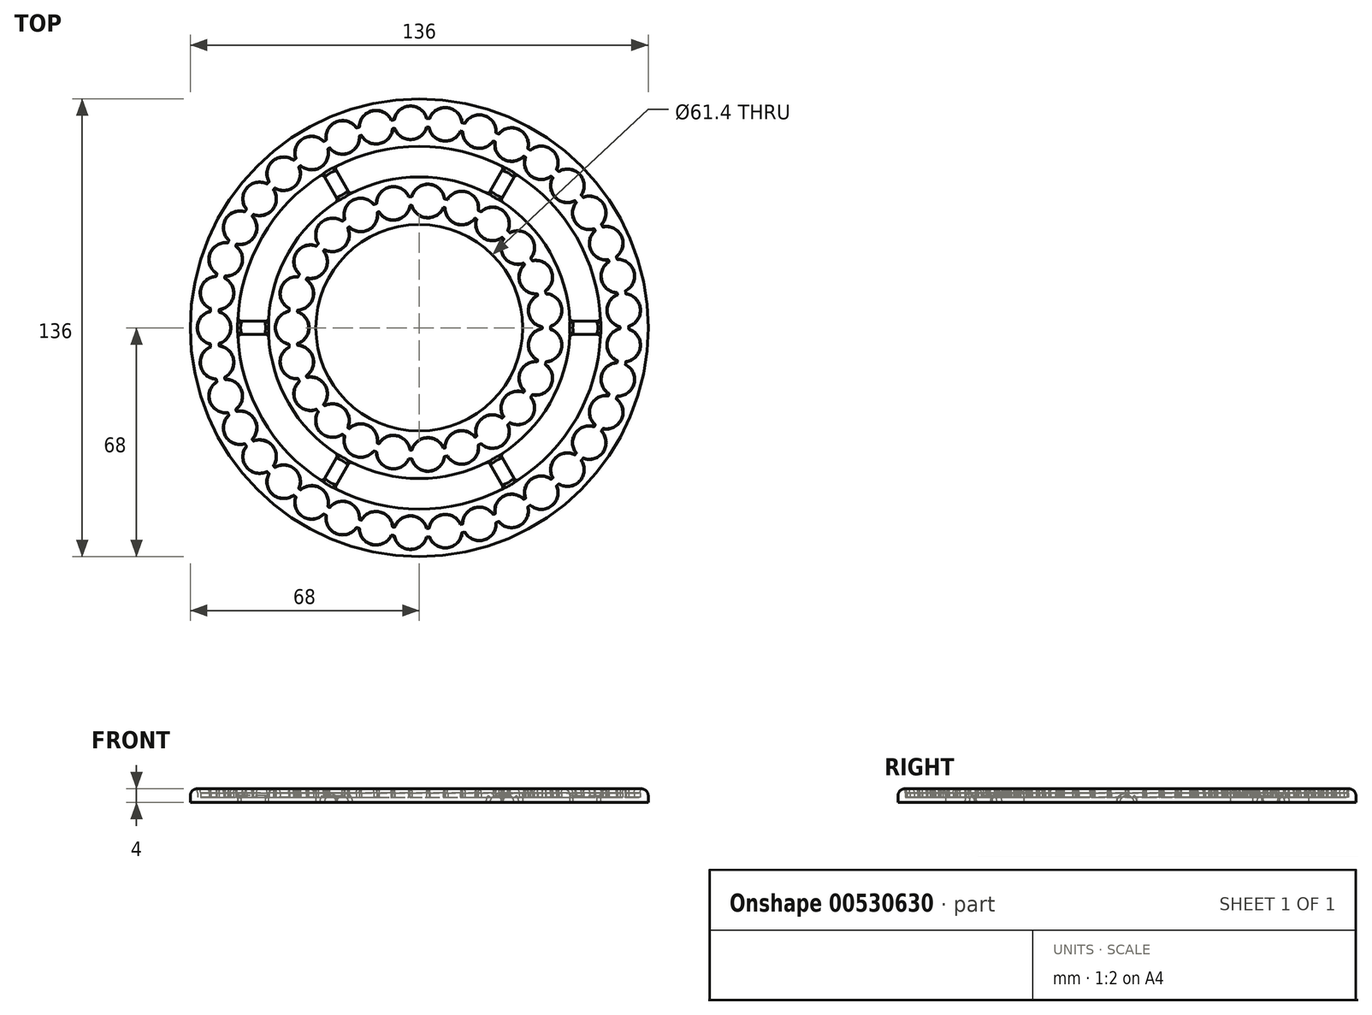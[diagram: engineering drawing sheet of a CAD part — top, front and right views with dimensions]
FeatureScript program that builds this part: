
annotation { "Feature Type Name" : "Feature", "Feature Type Description" : "" }
export const myFeature = defineFeature(function(context is Context, id is Id, definition is map)
    precondition{}
    {
        {
            var Q0;
            Q0=qCreatedBy(makeId("Front.planeOp"),FACE);
            var sketch = newSketch(context, id + "F0", { "sketchPlane" : qUnion([Q0])});
            skPoint(sketch, "E0", {"position": v(-70, 0) * mm});
            skLineSegment(sketch, "E1", {"start": v(-70, 0) * mm, "end": v(-70, 4) * mm});
            skLineSegment(sketch, "E2", {"start": v(-70, 4) * mm, "end": v(-66, 4) * mm});
            skLineSegment(sketch, "E3", {"start": v(-66, 4) * mm, "end": v(-65.85, 2.75) * mm});
            skLineSegment(sketch, "E4", {"start": v(-65.7, 1.5) * mm, "end": v(-56.2, 1.5) * mm});
            skLineSegment(sketch, "E5", {"start": v(-56.05, 2.75) * mm, "end": v(-55.9, 4) * mm});
            skLineSegment(sketch, "E6", {"start": v(-55.9, 4) * mm, "end": v(-42.8, 4) * mm});
            skLineSegment(sketch, "E7", {"start": v(-42.8, 4) * mm, "end": v(-42.65, 2.75) * mm});
            skLineSegment(sketch, "E8", {"start": v(-42.5, 1.5) * mm, "end": v(-33, 1.5) * mm});
            skLineSegment(sketch, "E9", {"start": v(-32.85, 2.75) * mm, "end": v(-32.7, 4) * mm});
            skLineSegment(sketch, "E10", {"start": v(-32.7, 4) * mm, "end": v(-28.7, 4) * mm});
            skLineSegment(sketch, "E11", {"start": v(-28.7, 4) * mm, "end": v(-28.7, 0) * mm});
            skLineSegment(sketch, "E12", {"start": v(-28.7, 0) * mm, "end": v(-70, 0) * mm});
            skPoint(sketch, "E13", {"position": v(-65.85, 2.75) * mm});
            skPoint(sketch, "E14", {"position": v(-32.85, 2.75) * mm});
            skLineSegment(sketch, "E15", {"start": v(-32.85, 2.75) * mm, "end": v(-32.85, 1.5) * mm});
            skLineSegment(sketch, "E16", {"start": v(-32.85, 1.5) * mm, "end": v(-33, 1.5) * mm});
            skLineSegment(sketch, "E17", {"start": v(-42.65, 2.75) * mm, "end": v(-42.65, 1.5) * mm});
            skLineSegment(sketch, "E18", {"start": v(-42.65, 1.5) * mm, "end": v(-42.5, 1.5) * mm});
            skLineSegment(sketch, "E19", {"start": v(-65.85, 2.75) * mm, "end": v(-65.85, 1.5) * mm});
            skLineSegment(sketch, "E20", {"start": v(-65.85, 1.5) * mm, "end": v(-65.7, 1.5) * mm});
            skLineSegment(sketch, "E21", {"start": v(-56.05, 2.75) * mm, "end": v(-56.05, 1.5) * mm});
            skLineSegment(sketch, "E22", {"start": v(-56.05, 1.5) * mm, "end": v(-56.2, 1.5) * mm});
            skLineSegment(sketch, "E23", {"start": v(0, 0) * mm, "end": v(0, 13.47) * mm});
            skLineSegment(sketch, "E24", {"start": v(-66, 4) * mm, "end": v(-32.7, 4) * mm});
            skLineSegment(sketch, "E25", {"start": v(-60.95, 1.5) * mm, "end": v(-60.95, 4) * mm});
            skLineSegment(sketch, "E26", {"start": v(-37.75, 1.5) * mm, "end": v(-37.75, 4) * mm});
            skLineSegment(sketch, "E27", {"start": v(-62.2, 1.5) * mm, "end": v(-62.2, 4) * mm});
            skLineSegment(sketch, "E28", {"start": v(-59.7, 4) * mm, "end": v(-59.7, 1.5) * mm});
            skLineSegment(sketch, "E29", {"start": v(-39, 4) * mm, "end": v(-39, 1.5) * mm});
            skLineSegment(sketch, "E30", {"start": v(-36.5, 4) * mm, "end": v(-36.5, 1.5) * mm});
            skPoint(sketch, "E31", {"position": v(-49.35, 4) * mm});
            skLineSegment(sketch, "E32", {"start": v(-68, 4) * mm, "end": v(-68, 0) * mm});
            skLineSegment(sketch, "E33", {"start": v(-30.7, 4) * mm, "end": v(-30.7, 0) * mm});
            skLineSegment(sketch, "E34", {"start": v(-53.9, 4) * mm, "end": v(-53.9, 2) * mm});
            skLineSegment(sketch, "E35", {"start": v(-53.9, 2) * mm, "end": v(-44.8, 2) * mm});
            skLineSegment(sketch, "E36", {"start": v(-44.8, 2) * mm, "end": v(-44.8, 4) * mm});
            skSolve(sketch);
        }
        {
            var Q0;
            {var subQ2=sQuery(id+"F0.wireOp",EDGE,"E9");Q0=makeQuery(id+"F0.imprint","IMPRINT",FACE,{"disambiguationData":[TD([[makeQuery(id+"F0.imprint","IMPRINT",EDGE,{"derivedFrom":subQ2}),1.0]])]});}
            var Q1;
            {var subQ1=sQuery(id+"F0.wireOp",EDGE,"E5");Q1=makeQuery(id+"F0.imprint","IMPRINT",FACE,{"disambiguationData":[TD([[makeQuery(id+"F0.imprint","IMPRINT",EDGE,{"derivedFrom":subQ1}),1.0]])]});}
            var Q2;
            {var subQ4=sQuery(id+"F0.wireOp",EDGE,"E3");Q2=makeQuery(id+"F0.imprint","IMPRINT",FACE,{"disambiguationData":[TD([[makeQuery(id+"F0.imprint","IMPRINT",EDGE,{"derivedFrom":subQ4}),1.0]])]});}
            var Q3;
            {var subQ3=sQuery(id+"F0.wireOp",EDGE,"E7");Q3=makeQuery(id+"F0.imprint","IMPRINT",FACE,{"disambiguationData":[TD([[makeQuery(id+"F0.imprint","IMPRINT",EDGE,{"derivedFrom":subQ3}),1.0]])]});}
            var Q4;
            {var subQ17=sQuery(id+"F0.wireOp",EDGE,"E3");Q4=makeQuery(id+"F0.imprint","IMPRINT",FACE,{"disambiguationData":[TD([[makeQuery(id+"F0.imprint","IMPRINT",EDGE,{"derivedFrom":subQ17}),-1.0]])]});}
            var Q5;
            Q5=sQuery(id+"F0.wireOp",EDGE,"E23");
            revolve(context, id + "F1", {"entities" : qUnion([Q0, Q1, Q2, Q3, Q4]), "axis" : qUnion([Q5]), "revolveType" : RevolveType.FULL});
        }
        {
            var Q0;
            {var subQ3=sQuery(id+"F0.wireOp",EDGE,"E3");Q0=makeQuery(id+"F0.imprint","IMPRINT",FACE,{"disambiguationData":[TD([[makeQuery(id+"F0.imprint","IMPRINT",EDGE,{"derivedFrom":subQ3}),1.0]])]});}
            var Q1;
            Q1=sQuery(id+"F0.wireOp",EDGE,"E25");
            revolve(context, id + "F2", {"entities" : qUnion([Q0]), "axis" : qUnion([Q1]), "revolveType" : RevolveType.FULL});
        }
        {
            var Q0;
            Q0=makeQuery(id+"F2.opRevolve","SWEPT_BODY",BODY,{"disambiguationData":[OSD([sQuery(id+"F0.wireOp",EDGE,"E3"),sQuery(id+"F0.wireOp",EDGE,"E4"),sQuery(id+"F0.wireOp",EDGE,"E19"),sQuery(id+"F0.wireOp",EDGE,"E20"),sQuery(id+"F0.wireOp",EDGE,"E24"),sQuery(id+"F0.wireOp",EDGE,"E25")])]});
            var Q1;
            Q1=sQuery(id+"F0.wireOp",EDGE,"E23");
            circularPattern(context, id + "F3", {"operationType" : NewBodyOperationType.REMOVE, "entities" : qUnion([Q0]), "axis" : qUnion([Q1]), "angle" : 360 * degree, "instanceCount" : 37, "equalSpace" : true});
        }
        {
            var Q0;
            {var subQ3=sQuery(id+"F0.wireOp",EDGE,"E7");Q0=makeQuery(id+"F0.imprint","IMPRINT",FACE,{"disambiguationData":[TD([[makeQuery(id+"F0.imprint","IMPRINT",EDGE,{"derivedFrom":subQ3}),1.0]])]});}
            var Q1;
            {var subQ0=sQuery(id+"F0.wireOp",EDGE,"E26");Q1=makeQuery(id+"F0.imprint","IMPRINT",FACE,{"disambiguationData":[TD([[makeQuery(id+"F0.imprint","IMPRINT",EDGE,{"derivedFrom":subQ0}),1.0]])]});}
            var Q2;
            Q2=sQuery(id+"F0.wireOp",EDGE,"E26");
            revolve(context, id + "F4", {"entities" : qUnion([Q0, Q1]), "axis" : qUnion([Q2]), "revolveType" : RevolveType.FULL});
        }
        {
            var Q0;
            Q0=makeQuery(id+"F4.opRevolve","SWEPT_BODY",BODY,{"disambiguationData":[OSD([sQuery(id+"F0.wireOp",EDGE,"E7"),sQuery(id+"F0.wireOp",EDGE,"E8"),sQuery(id+"F0.wireOp",EDGE,"E17"),sQuery(id+"F0.wireOp",EDGE,"E18"),sQuery(id+"F0.wireOp",EDGE,"E24"),sQuery(id+"F0.wireOp",EDGE,"E26")])]});
            var Q1;
            Q1=sQuery(id+"F0.wireOp",EDGE,"E23");
            circularPattern(context, id + "F5", {"operationType" : NewBodyOperationType.REMOVE, "entities" : qUnion([Q0]), "axis" : qUnion([Q1]), "angle" : 360 * degree, "instanceCount" : 23, "equalSpace" : true});
        }
        {
            var Q0;
            Q0=makeQuery(id+"F1.opRevolve","SWEPT_EDGE",EDGE,{"disambiguationData":[OSD([sQuery(id+"F0.wireOp",EDGE,"E1"),sQuery(id+"F0.wireOp",EDGE,"E2")])]});
            var Q1;
            Q1=makeQuery(id+"F1.opRevolve","SWEPT_EDGE",EDGE,{"disambiguationData":[OSD([sQuery(id+"F0.wireOp",EDGE,"E10"),sQuery(id+"F0.wireOp",EDGE,"E11")])]});
            fillet(context, id + "F6", {"entities" : qUnion([Q0, Q1]), "radius" : 2 * mm, "tangentPropagation" : true, "allowEdgeOverflow" : false});
        }
        {
            var Q0;
            Q0=qCreatedBy(makeId("Top.planeOp"),FACE);
            var sketch = newSketch(context, id + "F7", { "sketchPlane" : qUnion([Q0])});
            skCircle(sketch, "E37", {"center": v(0, 0) * mm, "radius": 49.35 * mm});
            skPoint(sketch, "E38", {"position": v(-49.35, 0) * mm});
            skCircle(sketch, "E39", {"center": v(0, 0) * mm, "radius": 44.8 * mm});
            skCircle(sketch, "E40", {"center": v(0, 0) * mm, "radius": 53.9 * mm});
            skPoint(sketch, "E41", {"position": v(-53.9, 0) * mm});
            skPoint(sketch, "E42", {"position": v(-44.8, 0) * mm});
            skLineSegment(sketch, "E43", {"start": v(-44.76, 2) * mm, "end": v(-53.86, 2) * mm});
            skLineSegment(sketch, "E44", {"start": v(-53.86, -2) * mm, "end": v(-44.76, -2) * mm});
            skPoint(sketch, "E45.1.0", {"position": v(-24.68, -42.74) * mm});
            skLineSegment(sketch, "E45.1.1", {"start": v(-25.2, -47.65) * mm, "end": v(-20.65, -39.76) * mm});
            skPoint(sketch, "E45.1.2", {"position": v(-22.4, -38.8) * mm});
            skLineSegment(sketch, "E45.1.3", {"start": v(-24.1, -37.76) * mm, "end": v(-28.66, -45.65) * mm});
            skPoint(sketch, "E45.1.4", {"position": v(-26.95, -46.68) * mm});
            skPoint(sketch, "E45.2.0", {"position": v(24.67, -42.74) * mm});
            skLineSegment(sketch, "E45.2.1", {"start": v(28.66, -45.65) * mm, "end": v(24.1, -37.76) * mm});
            skPoint(sketch, "E45.2.2", {"position": v(22.4, -38.8) * mm});
            skLineSegment(sketch, "E45.2.3", {"start": v(20.65, -39.76) * mm, "end": v(25.2, -47.65) * mm});
            skPoint(sketch, "E45.2.4", {"position": v(26.95, -46.68) * mm});
            skPoint(sketch, "E45.3.0", {"position": v(49.35, 0) * mm});
            skLineSegment(sketch, "E45.3.1", {"start": v(53.86, 2) * mm, "end": v(44.76, 2) * mm});
            skPoint(sketch, "E45.3.2", {"position": v(44.8, 0) * mm});
            skLineSegment(sketch, "E45.3.3", {"start": v(44.76, -2) * mm, "end": v(53.86, -2) * mm});
            skPoint(sketch, "E45.3.4", {"position": v(53.9, 0) * mm});
            skPoint(sketch, "E45.4.0", {"position": v(24.68, 42.74) * mm});
            skLineSegment(sketch, "E45.4.1", {"start": v(25.2, 47.65) * mm, "end": v(20.65, 39.76) * mm});
            skPoint(sketch, "E45.4.2", {"position": v(22.4, 38.8) * mm});
            skLineSegment(sketch, "E45.4.3", {"start": v(24.1, 37.76) * mm, "end": v(28.66, 45.65) * mm});
            skPoint(sketch, "E45.4.4", {"position": v(26.95, 46.68) * mm});
            skPoint(sketch, "E45.5.0", {"position": v(-24.68, 42.74) * mm});
            skLineSegment(sketch, "E45.5.1", {"start": v(-28.66, 45.65) * mm, "end": v(-24.1, 37.76) * mm});
            skPoint(sketch, "E45.5.2", {"position": v(-22.4, 38.8) * mm});
            skLineSegment(sketch, "E45.5.3", {"start": v(-20.65, 39.76) * mm, "end": v(-25.2, 47.65) * mm});
            skPoint(sketch, "E45.5.4", {"position": v(-26.95, 46.68) * mm});
            skSolve(sketch);
        }
        {
            var Q0;
            {var subQ0=sQuery(id+"F7.wireOp",EDGE,"E44");var subQ1=sQuery(id+"F7.wireOp",EDGE,"E37");var subQ2=makeQuery(id+"F7.imprint","INTERSECT",VERTEX,{"derivedFrom":[subQ1,subQ0]});Q0=makeQuery(id+"F7.imprint","IMPRINT",FACE,{"disambiguationData":[TD([[makeQuery(id+"F7.imprint","IMPRINT",EDGE,{"disambiguationData":[TD([[subQ2,-1.0]])],"derivedFrom":subQ1}),-1.0]])]});}
            var Q1;
            {var subQ0=sQuery(id+"F7.wireOp",EDGE,"E44");var subQ1=sQuery(id+"F7.wireOp",EDGE,"E37");var subQ2=makeQuery(id+"F7.imprint","INTERSECT",VERTEX,{"derivedFrom":[subQ1,subQ0]});Q1=makeQuery(id+"F7.imprint","IMPRINT",FACE,{"disambiguationData":[TD([[makeQuery(id+"F7.imprint","IMPRINT",EDGE,{"disambiguationData":[TD([[subQ2,-1.0]])],"derivedFrom":subQ1}),1.0]])]});}
            var Q2;
            {var subQ0=sQuery(id+"F7.wireOp",EDGE,"E45.1.1");var subQ1=sQuery(id+"F7.wireOp",EDGE,"E37");var subQ2=makeQuery(id+"F7.imprint","INTERSECT",VERTEX,{"derivedFrom":[subQ1,subQ0]});Q2=makeQuery(id+"F7.imprint","IMPRINT",FACE,{"disambiguationData":[TD([[makeQuery(id+"F7.imprint","IMPRINT",EDGE,{"disambiguationData":[TD([[subQ2,-1.0]])],"derivedFrom":subQ1}),1.0]])]});}
            var Q3;
            {var subQ0=sQuery(id+"F7.wireOp",EDGE,"E45.1.1");var subQ1=sQuery(id+"F7.wireOp",EDGE,"E37");var subQ2=makeQuery(id+"F7.imprint","INTERSECT",VERTEX,{"derivedFrom":[subQ1,subQ0]});Q3=makeQuery(id+"F7.imprint","IMPRINT",FACE,{"disambiguationData":[TD([[makeQuery(id+"F7.imprint","IMPRINT",EDGE,{"disambiguationData":[TD([[subQ2,-1.0]])],"derivedFrom":subQ1}),-1.0]])]});}
            var Q4;
            {var subQ0=sQuery(id+"F7.wireOp",EDGE,"E45.2.1");var subQ1=sQuery(id+"F7.wireOp",EDGE,"E37");var subQ2=makeQuery(id+"F7.imprint","INTERSECT",VERTEX,{"derivedFrom":[subQ1,subQ0]});Q4=makeQuery(id+"F7.imprint","IMPRINT",FACE,{"disambiguationData":[TD([[makeQuery(id+"F7.imprint","IMPRINT",EDGE,{"disambiguationData":[TD([[subQ2,-1.0]])],"derivedFrom":subQ1}),-1.0]])]});}
            var Q5;
            {var subQ0=sQuery(id+"F7.wireOp",EDGE,"E45.2.1");var subQ1=sQuery(id+"F7.wireOp",EDGE,"E37");var subQ2=makeQuery(id+"F7.imprint","INTERSECT",VERTEX,{"derivedFrom":[subQ1,subQ0]});Q5=makeQuery(id+"F7.imprint","IMPRINT",FACE,{"disambiguationData":[TD([[makeQuery(id+"F7.imprint","IMPRINT",EDGE,{"disambiguationData":[TD([[subQ2,-1.0]])],"derivedFrom":subQ1}),1.0]])]});}
            var Q6;
            {var subQ0=sQuery(id+"F7.wireOp",EDGE,"E45.4.3");var subQ1=sQuery(id+"F7.wireOp",EDGE,"E37");var subQ2=makeQuery(id+"F7.imprint","INTERSECT",VERTEX,{"derivedFrom":[subQ1,subQ0]});Q6=makeQuery(id+"F7.imprint","IMPRINT",FACE,{"disambiguationData":[TD([[makeQuery(id+"F7.imprint","IMPRINT",EDGE,{"disambiguationData":[TD([[subQ2,1.0]])],"derivedFrom":subQ1}),1.0]])]});}
            var Q7;
            {var subQ0=sQuery(id+"F7.wireOp",EDGE,"E45.4.3");var subQ1=sQuery(id+"F7.wireOp",EDGE,"E37");var subQ2=makeQuery(id+"F7.imprint","INTERSECT",VERTEX,{"derivedFrom":[subQ1,subQ0]});Q7=makeQuery(id+"F7.imprint","IMPRINT",FACE,{"disambiguationData":[TD([[makeQuery(id+"F7.imprint","IMPRINT",EDGE,{"disambiguationData":[TD([[subQ2,1.0]])],"derivedFrom":subQ1}),-1.0]])]});}
            var Q8;
            {var subQ0=sQuery(id+"F7.wireOp",EDGE,"E45.4.1");var subQ1=sQuery(id+"F7.wireOp",EDGE,"E37");var subQ2=makeQuery(id+"F7.imprint","INTERSECT",VERTEX,{"derivedFrom":[subQ1,subQ0]});Q8=makeQuery(id+"F7.imprint","IMPRINT",FACE,{"disambiguationData":[TD([[makeQuery(id+"F7.imprint","IMPRINT",EDGE,{"disambiguationData":[TD([[subQ2,-1.0]])],"derivedFrom":subQ1}),1.0]])]});}
            var Q9;
            {var subQ0=sQuery(id+"F7.wireOp",EDGE,"E45.4.1");var subQ1=sQuery(id+"F7.wireOp",EDGE,"E37");var subQ2=makeQuery(id+"F7.imprint","INTERSECT",VERTEX,{"derivedFrom":[subQ1,subQ0]});Q9=makeQuery(id+"F7.imprint","IMPRINT",FACE,{"disambiguationData":[TD([[makeQuery(id+"F7.imprint","IMPRINT",EDGE,{"disambiguationData":[TD([[subQ2,-1.0]])],"derivedFrom":subQ1}),-1.0]])]});}
            var Q10;
            {var subQ0=sQuery(id+"F7.wireOp",EDGE,"E45.5.1");var subQ1=sQuery(id+"F7.wireOp",EDGE,"E37");var subQ2=makeQuery(id+"F7.imprint","INTERSECT",VERTEX,{"derivedFrom":[subQ1,subQ0]});Q10=makeQuery(id+"F7.imprint","IMPRINT",FACE,{"disambiguationData":[TD([[makeQuery(id+"F7.imprint","IMPRINT",EDGE,{"disambiguationData":[TD([[subQ2,-1.0]])],"derivedFrom":subQ1}),-1.0]])]});}
            var Q11;
            {var subQ0=sQuery(id+"F7.wireOp",EDGE,"E45.5.1");var subQ1=sQuery(id+"F7.wireOp",EDGE,"E37");var subQ2=makeQuery(id+"F7.imprint","INTERSECT",VERTEX,{"derivedFrom":[subQ1,subQ0]});Q11=makeQuery(id+"F7.imprint","IMPRINT",FACE,{"disambiguationData":[TD([[makeQuery(id+"F7.imprint","IMPRINT",EDGE,{"disambiguationData":[TD([[subQ2,-1.0]])],"derivedFrom":subQ1}),1.0]])]});}
            extrude(context, id + "F8", {"entities" : qUnion([Q0, Q1, Q2, Q3, Q4, Q5, Q6, Q7, Q8, Q9, Q10, Q11]), "operationType" : NewBodyOperationType.REMOVE, "depth" : 25 * mm, "offsetDistance" : 25 * mm});
        }
        {
            var Q0;
            {var subQ0=sQuery(id+"F7.wireOp",EDGE,"E40");Q0=makeQuery(id+"F8.boolean.opBoolean","INTERSECT",EDGE,{"derivedFrom":[makeQuery(id+"F8.opExtrude","SWEPT_FACE",FACE,{"disambiguationData":[OSD([subQ0]),TDD([makeQuery(id+"F7.imprint","IMPRINT",EDGE,{"disambiguationData":[TD([[makeQuery(id+"F7.imprint","INTERSECT",VERTEX,{"derivedFrom":[subQ0,sQuery(id+"F7.wireOp",EDGE,"E45.3.1")]}),-1.0]])],"derivedFrom":subQ0})])]}),makeQuery(id+"F8.opExtrude","SWEPT_FACE",FACE,{"disambiguationData":[OSD([subQ0]),TDD([makeQuery(id+"F7.imprint","IMPRINT",EDGE,{"disambiguationData":[TD([[makeQuery(id+"F7.imprint","INTERSECT",VERTEX,{"derivedFrom":[subQ0,sQuery(id+"F7.wireOp",EDGE,"E45.4.1")]}),-1.0]])],"derivedFrom":subQ0})])]}),makeQuery(id+"F8.opExtrude","SWEPT_FACE",FACE,{"disambiguationData":[OSD([subQ0]),TDD([makeQuery(id+"F7.imprint","IMPRINT",EDGE,{"disambiguationData":[TD([[makeQuery(id+"F7.imprint","INTERSECT",VERTEX,{"derivedFrom":[subQ0,sQuery(id+"F7.wireOp",EDGE,"E43")]}),1.0]])],"derivedFrom":subQ0})])]}),makeQuery(id+"F8.opExtrude","SWEPT_FACE",FACE,{"disambiguationData":[OSD([subQ0]),TDD([makeQuery(id+"F7.imprint","IMPRINT",EDGE,{"disambiguationData":[TD([[makeQuery(id+"F7.imprint","INTERSECT",VERTEX,{"derivedFrom":[subQ0,sQuery(id+"F7.wireOp",EDGE,"E44")]}),-1.0]])],"derivedFrom":subQ0})])]}),makeQuery(id+"F8.opExtrude","SWEPT_FACE",FACE,{"disambiguationData":[OSD([subQ0]),TDD([makeQuery(id+"F7.imprint","IMPRINT",EDGE,{"disambiguationData":[TD([[makeQuery(id+"F7.imprint","INTERSECT",VERTEX,{"derivedFrom":[subQ0,sQuery(id+"F7.wireOp",EDGE,"E45.1.1")]}),-1.0]])],"derivedFrom":subQ0})])]}),makeQuery(id+"F8.opExtrude","SWEPT_FACE",FACE,{"disambiguationData":[OSD([subQ0]),TDD([makeQuery(id+"F7.imprint","IMPRINT",EDGE,{"disambiguationData":[TD([[makeQuery(id+"F7.imprint","INTERSECT",VERTEX,{"derivedFrom":[subQ0,sQuery(id+"F7.wireOp",EDGE,"E45.2.1")]}),-1.0]])],"derivedFrom":subQ0})])]})]});}
            var Q1;
            {var subQ0=sQuery(id+"F7.wireOp",EDGE,"E39");Q1=makeQuery(id+"F8.boolean.opBoolean","INTERSECT",EDGE,{"derivedFrom":[makeQuery(id+"F8.opExtrude","SWEPT_FACE",FACE,{"disambiguationData":[OSD([subQ0]),TDD([makeQuery(id+"F7.imprint","IMPRINT",EDGE,{"disambiguationData":[TD([[makeQuery(id+"F7.imprint","INTERSECT",VERTEX,{"derivedFrom":[subQ0,sQuery(id+"F7.wireOp",EDGE,"E45.3.1")]}),-1.0]])],"derivedFrom":subQ0})])]}),makeQuery(id+"F8.opExtrude","SWEPT_FACE",FACE,{"disambiguationData":[OSD([subQ0]),TDD([makeQuery(id+"F7.imprint","IMPRINT",EDGE,{"disambiguationData":[TD([[makeQuery(id+"F7.imprint","INTERSECT",VERTEX,{"derivedFrom":[subQ0,sQuery(id+"F7.wireOp",EDGE,"E45.4.1")]}),-1.0]])],"derivedFrom":subQ0})])]}),makeQuery(id+"F8.opExtrude","SWEPT_FACE",FACE,{"disambiguationData":[OSD([subQ0]),TDD([makeQuery(id+"F7.imprint","IMPRINT",EDGE,{"disambiguationData":[TD([[makeQuery(id+"F7.imprint","INTERSECT",VERTEX,{"derivedFrom":[subQ0,sQuery(id+"F7.wireOp",EDGE,"E43")]}),1.0]])],"derivedFrom":subQ0})])]}),makeQuery(id+"F8.opExtrude","SWEPT_FACE",FACE,{"disambiguationData":[OSD([subQ0]),TDD([makeQuery(id+"F7.imprint","IMPRINT",EDGE,{"disambiguationData":[TD([[makeQuery(id+"F7.imprint","INTERSECT",VERTEX,{"derivedFrom":[subQ0,sQuery(id+"F7.wireOp",EDGE,"E44")]}),-1.0]])],"derivedFrom":subQ0})])]}),makeQuery(id+"F8.opExtrude","SWEPT_FACE",FACE,{"disambiguationData":[OSD([subQ0]),TDD([makeQuery(id+"F7.imprint","IMPRINT",EDGE,{"disambiguationData":[TD([[makeQuery(id+"F7.imprint","INTERSECT",VERTEX,{"derivedFrom":[subQ0,sQuery(id+"F7.wireOp",EDGE,"E45.1.1")]}),-1.0]])],"derivedFrom":subQ0})])]}),makeQuery(id+"F8.opExtrude","SWEPT_FACE",FACE,{"disambiguationData":[OSD([subQ0]),TDD([makeQuery(id+"F7.imprint","IMPRINT",EDGE,{"disambiguationData":[TD([[makeQuery(id+"F7.imprint","INTERSECT",VERTEX,{"derivedFrom":[subQ0,sQuery(id+"F7.wireOp",EDGE,"E45.2.1")]}),-1.0]])],"derivedFrom":subQ0})])]})]});}
            fillet(context, id + "F9", {"entities" : qUnion([Q0, Q1]), "radius" : 2 * mm, "tangentPropagation" : true, "allowEdgeOverflow" : false});
        }
        {
            var Q0;
            Q0=makeQuery(id+"F8.boolean.opBoolean","INTERSECT",EDGE,{"derivedFrom":[makeQuery(id+"F1.opRevolve","SWEPT_FACE",FACE,{"disambiguationData":[OSD([sQuery(id+"F0.wireOp",EDGE,"E35")])]}),makeQuery(id+"F8.opExtrude","SWEPT_FACE",FACE,{"disambiguationData":[OSD([sQuery(id+"F7.wireOp",EDGE,"E43")])]})]});
            var Q1;
            Q1=makeQuery(id+"F8.boolean.opBoolean","INTERSECT",EDGE,{"derivedFrom":[makeQuery(id+"F1.opRevolve","SWEPT_FACE",FACE,{"disambiguationData":[OSD([sQuery(id+"F0.wireOp",EDGE,"E35")])]}),makeQuery(id+"F8.opExtrude","SWEPT_FACE",FACE,{"disambiguationData":[OSD([sQuery(id+"F7.wireOp",EDGE,"E44")])]})]});
            var Q2;
            Q2=makeQuery(id+"F8.boolean.opBoolean","INTERSECT",EDGE,{"derivedFrom":[makeQuery(id+"F1.opRevolve","SWEPT_FACE",FACE,{"disambiguationData":[OSD([sQuery(id+"F0.wireOp",EDGE,"E35")])]}),makeQuery(id+"F8.opExtrude","SWEPT_FACE",FACE,{"disambiguationData":[OSD([sQuery(id+"F7.wireOp",EDGE,"E45.1.3")])]})]});
            var Q3;
            Q3=makeQuery(id+"F8.boolean.opBoolean","INTERSECT",EDGE,{"derivedFrom":[makeQuery(id+"F1.opRevolve","SWEPT_FACE",FACE,{"disambiguationData":[OSD([sQuery(id+"F0.wireOp",EDGE,"E35")])]}),makeQuery(id+"F8.opExtrude","SWEPT_FACE",FACE,{"disambiguationData":[OSD([sQuery(id+"F7.wireOp",EDGE,"E45.1.1")])]})]});
            var Q4;
            Q4=makeQuery(id+"F8.boolean.opBoolean","INTERSECT",EDGE,{"derivedFrom":[makeQuery(id+"F1.opRevolve","SWEPT_FACE",FACE,{"disambiguationData":[OSD([sQuery(id+"F0.wireOp",EDGE,"E35")])]}),makeQuery(id+"F8.opExtrude","SWEPT_FACE",FACE,{"disambiguationData":[OSD([sQuery(id+"F7.wireOp",EDGE,"E45.2.3")])]})]});
            var Q5;
            Q5=makeQuery(id+"F8.boolean.opBoolean","INTERSECT",EDGE,{"derivedFrom":[makeQuery(id+"F1.opRevolve","SWEPT_FACE",FACE,{"disambiguationData":[OSD([sQuery(id+"F0.wireOp",EDGE,"E35")])]}),makeQuery(id+"F8.opExtrude","SWEPT_FACE",FACE,{"disambiguationData":[OSD([sQuery(id+"F7.wireOp",EDGE,"E45.2.1")])]})]});
            var Q6;
            Q6=makeQuery(id+"F8.boolean.opBoolean","INTERSECT",EDGE,{"derivedFrom":[makeQuery(id+"F1.opRevolve","SWEPT_FACE",FACE,{"disambiguationData":[OSD([sQuery(id+"F0.wireOp",EDGE,"E35")])]}),makeQuery(id+"F8.opExtrude","SWEPT_FACE",FACE,{"disambiguationData":[OSD([sQuery(id+"F7.wireOp",EDGE,"E45.3.3")])]})]});
            var Q7;
            Q7=makeQuery(id+"F8.boolean.opBoolean","INTERSECT",EDGE,{"derivedFrom":[makeQuery(id+"F1.opRevolve","SWEPT_FACE",FACE,{"disambiguationData":[OSD([sQuery(id+"F0.wireOp",EDGE,"E35")])]}),makeQuery(id+"F8.opExtrude","SWEPT_FACE",FACE,{"disambiguationData":[OSD([sQuery(id+"F7.wireOp",EDGE,"E45.3.1")])]})]});
            var Q8;
            Q8=makeQuery(id+"F8.boolean.opBoolean","INTERSECT",EDGE,{"derivedFrom":[makeQuery(id+"F1.opRevolve","SWEPT_FACE",FACE,{"disambiguationData":[OSD([sQuery(id+"F0.wireOp",EDGE,"E35")])]}),makeQuery(id+"F8.opExtrude","SWEPT_FACE",FACE,{"disambiguationData":[OSD([sQuery(id+"F7.wireOp",EDGE,"E45.4.3")])]})]});
            var Q9;
            Q9=makeQuery(id+"F8.boolean.opBoolean","INTERSECT",EDGE,{"derivedFrom":[makeQuery(id+"F1.opRevolve","SWEPT_FACE",FACE,{"disambiguationData":[OSD([sQuery(id+"F0.wireOp",EDGE,"E35")])]}),makeQuery(id+"F8.opExtrude","SWEPT_FACE",FACE,{"disambiguationData":[OSD([sQuery(id+"F7.wireOp",EDGE,"E45.5.1")])]})]});
            var Q10;
            Q10=makeQuery(id+"F8.boolean.opBoolean","INTERSECT",EDGE,{"derivedFrom":[makeQuery(id+"F1.opRevolve","SWEPT_FACE",FACE,{"disambiguationData":[OSD([sQuery(id+"F0.wireOp",EDGE,"E35")])]}),makeQuery(id+"F8.opExtrude","SWEPT_FACE",FACE,{"disambiguationData":[OSD([sQuery(id+"F7.wireOp",EDGE,"E45.5.3")])]})]});
            var Q11;
            Q11=makeQuery(id+"F8.boolean.opBoolean","INTERSECT",EDGE,{"derivedFrom":[makeQuery(id+"F1.opRevolve","SWEPT_FACE",FACE,{"disambiguationData":[OSD([sQuery(id+"F0.wireOp",EDGE,"E35")])]}),makeQuery(id+"F8.opExtrude","SWEPT_FACE",FACE,{"disambiguationData":[OSD([sQuery(id+"F7.wireOp",EDGE,"E45.4.1")])]})]});
            fillet(context, id + "F10", {"entities" : qUnion([Q0, Q1, Q2, Q3, Q4, Q5, Q6, Q7, Q8, Q9, Q10, Q11]), "radius" : 2 * mm, "tangentPropagation" : true, "allowEdgeOverflow" : false});
        }
        {
            var Q0;
            {var subQ0=sQuery(id+"F7.wireOp",EDGE,"E40");var subQ1=sQuery(id+"F7.wireOp",EDGE,"E44");Q0=makeQuery(id+"F10.opFillet","BLEND_EDGE",EDGE,{"blendedFrom":[makeQuery(id+"F8.boolean.opBoolean","INTERSECT",EDGE,{"derivedFrom":[makeQuery(id+"F1.opRevolve","SWEPT_FACE",FACE,{"disambiguationData":[OSD([sQuery(id+"F0.wireOp",EDGE,"E35")])]}),makeQuery(id+"F8.opExtrude","SWEPT_FACE",FACE,{"disambiguationData":[OSD([subQ1])]})]}),makeQuery(id+"F9.opFillet","SPLIT",FACE,{"disambiguationData":[OD(1.0)],"derivedFrom":makeQuery(id+"F8.boolean.opBoolean","MERGE",FACE,{"derivedFrom":[makeQuery(id+"F1.opRevolve","SWEPT_FACE",FACE,{"disambiguationData":[OSD([sQuery(id+"F0.wireOp",EDGE,"E34")])]}),makeQuery(id+"F8.opExtrude","SWEPT_FACE",FACE,{"disambiguationData":[OSD([subQ0]),TDD([makeQuery(id+"F7.imprint","IMPRINT",EDGE,{"disambiguationData":[TD([[makeQuery(id+"F7.imprint","INTERSECT",VERTEX,{"derivedFrom":[subQ0,sQuery(id+"F7.wireOp",EDGE,"E45.3.1")]}),-1.0]])],"derivedFrom":subQ0})])]}),makeQuery(id+"F8.opExtrude","SWEPT_FACE",FACE,{"disambiguationData":[OSD([subQ0]),TDD([makeQuery(id+"F7.imprint","IMPRINT",EDGE,{"disambiguationData":[TD([[makeQuery(id+"F7.imprint","INTERSECT",VERTEX,{"derivedFrom":[subQ0,sQuery(id+"F7.wireOp",EDGE,"E45.4.1")]}),-1.0]])],"derivedFrom":subQ0})])]}),makeQuery(id+"F8.opExtrude","SWEPT_FACE",FACE,{"disambiguationData":[OSD([subQ0]),TDD([makeQuery(id+"F7.imprint","IMPRINT",EDGE,{"disambiguationData":[TD([[makeQuery(id+"F7.imprint","INTERSECT",VERTEX,{"derivedFrom":[subQ0,sQuery(id+"F7.wireOp",EDGE,"E43")]}),1.0]])],"derivedFrom":subQ0})])]}),makeQuery(id+"F8.opExtrude","SWEPT_FACE",FACE,{"disambiguationData":[OSD([subQ0]),TDD([makeQuery(id+"F7.imprint","IMPRINT",EDGE,{"disambiguationData":[TD([[makeQuery(id+"F7.imprint","INTERSECT",VERTEX,{"derivedFrom":[subQ0,subQ1]}),-1.0]])],"derivedFrom":subQ0})])]}),makeQuery(id+"F8.opExtrude","SWEPT_FACE",FACE,{"disambiguationData":[OSD([subQ0]),TDD([makeQuery(id+"F7.imprint","IMPRINT",EDGE,{"disambiguationData":[TD([[makeQuery(id+"F7.imprint","INTERSECT",VERTEX,{"derivedFrom":[subQ0,sQuery(id+"F7.wireOp",EDGE,"E45.1.1")]}),-1.0]])],"derivedFrom":subQ0})])]}),makeQuery(id+"F8.opExtrude","SWEPT_FACE",FACE,{"disambiguationData":[OSD([subQ0]),TDD([makeQuery(id+"F7.imprint","IMPRINT",EDGE,{"disambiguationData":[TD([[makeQuery(id+"F7.imprint","INTERSECT",VERTEX,{"derivedFrom":[subQ0,sQuery(id+"F7.wireOp",EDGE,"E45.2.1")]}),-1.0]])],"derivedFrom":subQ0})])]})]})})],"blendedInto":[makeQuery(id+"F9.opFillet","SPLIT",FACE,{"disambiguationData":[OD(1.0)],"derivedFrom":makeQuery(id+"F8.boolean.opBoolean","MERGE",FACE,{"derivedFrom":[makeQuery(id+"F1.opRevolve","SWEPT_FACE",FACE,{"disambiguationData":[OSD([sQuery(id+"F0.wireOp",EDGE,"E34")])]}),makeQuery(id+"F8.opExtrude","SWEPT_FACE",FACE,{"disambiguationData":[OSD([subQ0]),TDD([makeQuery(id+"F7.imprint","IMPRINT",EDGE,{"disambiguationData":[TD([[makeQuery(id+"F7.imprint","INTERSECT",VERTEX,{"derivedFrom":[subQ0,sQuery(id+"F7.wireOp",EDGE,"E45.3.1")]}),-1.0]])],"derivedFrom":subQ0})])]}),makeQuery(id+"F8.opExtrude","SWEPT_FACE",FACE,{"disambiguationData":[OSD([subQ0]),TDD([makeQuery(id+"F7.imprint","IMPRINT",EDGE,{"disambiguationData":[TD([[makeQuery(id+"F7.imprint","INTERSECT",VERTEX,{"derivedFrom":[subQ0,sQuery(id+"F7.wireOp",EDGE,"E45.4.1")]}),-1.0]])],"derivedFrom":subQ0})])]}),makeQuery(id+"F8.opExtrude","SWEPT_FACE",FACE,{"disambiguationData":[OSD([subQ0]),TDD([makeQuery(id+"F7.imprint","IMPRINT",EDGE,{"disambiguationData":[TD([[makeQuery(id+"F7.imprint","INTERSECT",VERTEX,{"derivedFrom":[subQ0,sQuery(id+"F7.wireOp",EDGE,"E43")]}),1.0]])],"derivedFrom":subQ0})])]}),makeQuery(id+"F8.opExtrude","SWEPT_FACE",FACE,{"disambiguationData":[OSD([subQ0]),TDD([makeQuery(id+"F7.imprint","IMPRINT",EDGE,{"disambiguationData":[TD([[makeQuery(id+"F7.imprint","INTERSECT",VERTEX,{"derivedFrom":[subQ0,subQ1]}),-1.0]])],"derivedFrom":subQ0})])]}),makeQuery(id+"F8.opExtrude","SWEPT_FACE",FACE,{"disambiguationData":[OSD([subQ0]),TDD([makeQuery(id+"F7.imprint","IMPRINT",EDGE,{"disambiguationData":[TD([[makeQuery(id+"F7.imprint","INTERSECT",VERTEX,{"derivedFrom":[subQ0,sQuery(id+"F7.wireOp",EDGE,"E45.1.1")]}),-1.0]])],"derivedFrom":subQ0})])]}),makeQuery(id+"F8.opExtrude","SWEPT_FACE",FACE,{"disambiguationData":[OSD([subQ0]),TDD([makeQuery(id+"F7.imprint","IMPRINT",EDGE,{"disambiguationData":[TD([[makeQuery(id+"F7.imprint","INTERSECT",VERTEX,{"derivedFrom":[subQ0,sQuery(id+"F7.wireOp",EDGE,"E45.2.1")]}),-1.0]])],"derivedFrom":subQ0})])]})]})})]});}
            var Q1;
            {var subQ0=sQuery(id+"F7.wireOp",EDGE,"E39");var subQ1=sQuery(id+"F7.wireOp",EDGE,"E44");Q1=makeQuery(id+"F10.opFillet","BLEND_EDGE",EDGE,{"blendedFrom":[makeQuery(id+"F8.boolean.opBoolean","INTERSECT",EDGE,{"derivedFrom":[makeQuery(id+"F1.opRevolve","SWEPT_FACE",FACE,{"disambiguationData":[OSD([sQuery(id+"F0.wireOp",EDGE,"E35")])]}),makeQuery(id+"F8.opExtrude","SWEPT_FACE",FACE,{"disambiguationData":[OSD([subQ1])]})]}),makeQuery(id+"F9.opFillet","SPLIT",FACE,{"disambiguationData":[OD(1.0)],"derivedFrom":makeQuery(id+"F8.boolean.opBoolean","MERGE",FACE,{"derivedFrom":[makeQuery(id+"F1.opRevolve","SWEPT_FACE",FACE,{"disambiguationData":[OSD([sQuery(id+"F0.wireOp",EDGE,"E36")])]}),makeQuery(id+"F8.opExtrude","SWEPT_FACE",FACE,{"disambiguationData":[OSD([subQ0]),TDD([makeQuery(id+"F7.imprint","IMPRINT",EDGE,{"disambiguationData":[TD([[makeQuery(id+"F7.imprint","INTERSECT",VERTEX,{"derivedFrom":[subQ0,sQuery(id+"F7.wireOp",EDGE,"E45.3.1")]}),-1.0]])],"derivedFrom":subQ0})])]}),makeQuery(id+"F8.opExtrude","SWEPT_FACE",FACE,{"disambiguationData":[OSD([subQ0]),TDD([makeQuery(id+"F7.imprint","IMPRINT",EDGE,{"disambiguationData":[TD([[makeQuery(id+"F7.imprint","INTERSECT",VERTEX,{"derivedFrom":[subQ0,sQuery(id+"F7.wireOp",EDGE,"E45.4.1")]}),-1.0]])],"derivedFrom":subQ0})])]}),makeQuery(id+"F8.opExtrude","SWEPT_FACE",FACE,{"disambiguationData":[OSD([subQ0]),TDD([makeQuery(id+"F7.imprint","IMPRINT",EDGE,{"disambiguationData":[TD([[makeQuery(id+"F7.imprint","INTERSECT",VERTEX,{"derivedFrom":[subQ0,sQuery(id+"F7.wireOp",EDGE,"E43")]}),1.0]])],"derivedFrom":subQ0})])]}),makeQuery(id+"F8.opExtrude","SWEPT_FACE",FACE,{"disambiguationData":[OSD([subQ0]),TDD([makeQuery(id+"F7.imprint","IMPRINT",EDGE,{"disambiguationData":[TD([[makeQuery(id+"F7.imprint","INTERSECT",VERTEX,{"derivedFrom":[subQ0,subQ1]}),-1.0]])],"derivedFrom":subQ0})])]}),makeQuery(id+"F8.opExtrude","SWEPT_FACE",FACE,{"disambiguationData":[OSD([subQ0]),TDD([makeQuery(id+"F7.imprint","IMPRINT",EDGE,{"disambiguationData":[TD([[makeQuery(id+"F7.imprint","INTERSECT",VERTEX,{"derivedFrom":[subQ0,sQuery(id+"F7.wireOp",EDGE,"E45.1.1")]}),-1.0]])],"derivedFrom":subQ0})])]}),makeQuery(id+"F8.opExtrude","SWEPT_FACE",FACE,{"disambiguationData":[OSD([subQ0]),TDD([makeQuery(id+"F7.imprint","IMPRINT",EDGE,{"disambiguationData":[TD([[makeQuery(id+"F7.imprint","INTERSECT",VERTEX,{"derivedFrom":[subQ0,sQuery(id+"F7.wireOp",EDGE,"E45.2.1")]}),-1.0]])],"derivedFrom":subQ0})])]})]})})],"blendedInto":[makeQuery(id+"F9.opFillet","SPLIT",FACE,{"disambiguationData":[OD(1.0)],"derivedFrom":makeQuery(id+"F8.boolean.opBoolean","MERGE",FACE,{"derivedFrom":[makeQuery(id+"F1.opRevolve","SWEPT_FACE",FACE,{"disambiguationData":[OSD([sQuery(id+"F0.wireOp",EDGE,"E36")])]}),makeQuery(id+"F8.opExtrude","SWEPT_FACE",FACE,{"disambiguationData":[OSD([subQ0]),TDD([makeQuery(id+"F7.imprint","IMPRINT",EDGE,{"disambiguationData":[TD([[makeQuery(id+"F7.imprint","INTERSECT",VERTEX,{"derivedFrom":[subQ0,sQuery(id+"F7.wireOp",EDGE,"E45.3.1")]}),-1.0]])],"derivedFrom":subQ0})])]}),makeQuery(id+"F8.opExtrude","SWEPT_FACE",FACE,{"disambiguationData":[OSD([subQ0]),TDD([makeQuery(id+"F7.imprint","IMPRINT",EDGE,{"disambiguationData":[TD([[makeQuery(id+"F7.imprint","INTERSECT",VERTEX,{"derivedFrom":[subQ0,sQuery(id+"F7.wireOp",EDGE,"E45.4.1")]}),-1.0]])],"derivedFrom":subQ0})])]}),makeQuery(id+"F8.opExtrude","SWEPT_FACE",FACE,{"disambiguationData":[OSD([subQ0]),TDD([makeQuery(id+"F7.imprint","IMPRINT",EDGE,{"disambiguationData":[TD([[makeQuery(id+"F7.imprint","INTERSECT",VERTEX,{"derivedFrom":[subQ0,sQuery(id+"F7.wireOp",EDGE,"E43")]}),1.0]])],"derivedFrom":subQ0})])]}),makeQuery(id+"F8.opExtrude","SWEPT_FACE",FACE,{"disambiguationData":[OSD([subQ0]),TDD([makeQuery(id+"F7.imprint","IMPRINT",EDGE,{"disambiguationData":[TD([[makeQuery(id+"F7.imprint","INTERSECT",VERTEX,{"derivedFrom":[subQ0,subQ1]}),-1.0]])],"derivedFrom":subQ0})])]}),makeQuery(id+"F8.opExtrude","SWEPT_FACE",FACE,{"disambiguationData":[OSD([subQ0]),TDD([makeQuery(id+"F7.imprint","IMPRINT",EDGE,{"disambiguationData":[TD([[makeQuery(id+"F7.imprint","INTERSECT",VERTEX,{"derivedFrom":[subQ0,sQuery(id+"F7.wireOp",EDGE,"E45.1.1")]}),-1.0]])],"derivedFrom":subQ0})])]}),makeQuery(id+"F8.opExtrude","SWEPT_FACE",FACE,{"disambiguationData":[OSD([subQ0]),TDD([makeQuery(id+"F7.imprint","IMPRINT",EDGE,{"disambiguationData":[TD([[makeQuery(id+"F7.imprint","INTERSECT",VERTEX,{"derivedFrom":[subQ0,sQuery(id+"F7.wireOp",EDGE,"E45.2.1")]}),-1.0]])],"derivedFrom":subQ0})])]})]})})]});}
            var Q2;
            {var subQ0=sQuery(id+"F7.wireOp",EDGE,"E40");var subQ1=sQuery(id+"F7.wireOp",EDGE,"E45.5.1");Q2=makeQuery(id+"F10.opFillet","BLEND_EDGE",EDGE,{"blendedFrom":[makeQuery(id+"F8.boolean.opBoolean","INTERSECT",EDGE,{"derivedFrom":[makeQuery(id+"F1.opRevolve","SWEPT_FACE",FACE,{"disambiguationData":[OSD([sQuery(id+"F0.wireOp",EDGE,"E35")])]}),makeQuery(id+"F8.opExtrude","SWEPT_FACE",FACE,{"disambiguationData":[OSD([subQ1])]})]}),makeQuery(id+"F9.opFillet","SPLIT",FACE,{"disambiguationData":[OD(0.0)],"derivedFrom":makeQuery(id+"F8.boolean.opBoolean","MERGE",FACE,{"derivedFrom":[makeQuery(id+"F1.opRevolve","SWEPT_FACE",FACE,{"disambiguationData":[OSD([sQuery(id+"F0.wireOp",EDGE,"E34")])]}),makeQuery(id+"F8.opExtrude","SWEPT_FACE",FACE,{"disambiguationData":[OSD([subQ0]),TDD([makeQuery(id+"F7.imprint","IMPRINT",EDGE,{"disambiguationData":[TD([[makeQuery(id+"F7.imprint","INTERSECT",VERTEX,{"derivedFrom":[subQ0,sQuery(id+"F7.wireOp",EDGE,"E45.3.1")]}),-1.0]])],"derivedFrom":subQ0})])]}),makeQuery(id+"F8.opExtrude","SWEPT_FACE",FACE,{"disambiguationData":[OSD([subQ0]),TDD([makeQuery(id+"F7.imprint","IMPRINT",EDGE,{"disambiguationData":[TD([[makeQuery(id+"F7.imprint","INTERSECT",VERTEX,{"derivedFrom":[subQ0,sQuery(id+"F7.wireOp",EDGE,"E45.4.1")]}),-1.0]])],"derivedFrom":subQ0})])]}),makeQuery(id+"F8.opExtrude","SWEPT_FACE",FACE,{"disambiguationData":[OSD([subQ0]),TDD([makeQuery(id+"F7.imprint","IMPRINT",EDGE,{"disambiguationData":[TD([[makeQuery(id+"F7.imprint","INTERSECT",VERTEX,{"derivedFrom":[subQ0,sQuery(id+"F7.wireOp",EDGE,"E43")]}),1.0]])],"derivedFrom":subQ0})])]}),makeQuery(id+"F8.opExtrude","SWEPT_FACE",FACE,{"disambiguationData":[OSD([subQ0]),TDD([makeQuery(id+"F7.imprint","IMPRINT",EDGE,{"disambiguationData":[TD([[makeQuery(id+"F7.imprint","INTERSECT",VERTEX,{"derivedFrom":[subQ0,sQuery(id+"F7.wireOp",EDGE,"E44")]}),-1.0]])],"derivedFrom":subQ0})])]}),makeQuery(id+"F8.opExtrude","SWEPT_FACE",FACE,{"disambiguationData":[OSD([subQ0]),TDD([makeQuery(id+"F7.imprint","IMPRINT",EDGE,{"disambiguationData":[TD([[makeQuery(id+"F7.imprint","INTERSECT",VERTEX,{"derivedFrom":[subQ0,sQuery(id+"F7.wireOp",EDGE,"E45.1.1")]}),-1.0]])],"derivedFrom":subQ0})])]}),makeQuery(id+"F8.opExtrude","SWEPT_FACE",FACE,{"disambiguationData":[OSD([subQ0]),TDD([makeQuery(id+"F7.imprint","IMPRINT",EDGE,{"disambiguationData":[TD([[makeQuery(id+"F7.imprint","INTERSECT",VERTEX,{"derivedFrom":[subQ0,sQuery(id+"F7.wireOp",EDGE,"E45.2.1")]}),-1.0]])],"derivedFrom":subQ0})])]})]})})],"blendedInto":[makeQuery(id+"F9.opFillet","SPLIT",FACE,{"disambiguationData":[OD(0.0)],"derivedFrom":makeQuery(id+"F8.boolean.opBoolean","MERGE",FACE,{"derivedFrom":[makeQuery(id+"F1.opRevolve","SWEPT_FACE",FACE,{"disambiguationData":[OSD([sQuery(id+"F0.wireOp",EDGE,"E34")])]}),makeQuery(id+"F8.opExtrude","SWEPT_FACE",FACE,{"disambiguationData":[OSD([subQ0]),TDD([makeQuery(id+"F7.imprint","IMPRINT",EDGE,{"disambiguationData":[TD([[makeQuery(id+"F7.imprint","INTERSECT",VERTEX,{"derivedFrom":[subQ0,sQuery(id+"F7.wireOp",EDGE,"E45.3.1")]}),-1.0]])],"derivedFrom":subQ0})])]}),makeQuery(id+"F8.opExtrude","SWEPT_FACE",FACE,{"disambiguationData":[OSD([subQ0]),TDD([makeQuery(id+"F7.imprint","IMPRINT",EDGE,{"disambiguationData":[TD([[makeQuery(id+"F7.imprint","INTERSECT",VERTEX,{"derivedFrom":[subQ0,sQuery(id+"F7.wireOp",EDGE,"E45.4.1")]}),-1.0]])],"derivedFrom":subQ0})])]}),makeQuery(id+"F8.opExtrude","SWEPT_FACE",FACE,{"disambiguationData":[OSD([subQ0]),TDD([makeQuery(id+"F7.imprint","IMPRINT",EDGE,{"disambiguationData":[TD([[makeQuery(id+"F7.imprint","INTERSECT",VERTEX,{"derivedFrom":[subQ0,sQuery(id+"F7.wireOp",EDGE,"E43")]}),1.0]])],"derivedFrom":subQ0})])]}),makeQuery(id+"F8.opExtrude","SWEPT_FACE",FACE,{"disambiguationData":[OSD([subQ0]),TDD([makeQuery(id+"F7.imprint","IMPRINT",EDGE,{"disambiguationData":[TD([[makeQuery(id+"F7.imprint","INTERSECT",VERTEX,{"derivedFrom":[subQ0,sQuery(id+"F7.wireOp",EDGE,"E44")]}),-1.0]])],"derivedFrom":subQ0})])]}),makeQuery(id+"F8.opExtrude","SWEPT_FACE",FACE,{"disambiguationData":[OSD([subQ0]),TDD([makeQuery(id+"F7.imprint","IMPRINT",EDGE,{"disambiguationData":[TD([[makeQuery(id+"F7.imprint","INTERSECT",VERTEX,{"derivedFrom":[subQ0,sQuery(id+"F7.wireOp",EDGE,"E45.1.1")]}),-1.0]])],"derivedFrom":subQ0})])]}),makeQuery(id+"F8.opExtrude","SWEPT_FACE",FACE,{"disambiguationData":[OSD([subQ0]),TDD([makeQuery(id+"F7.imprint","IMPRINT",EDGE,{"disambiguationData":[TD([[makeQuery(id+"F7.imprint","INTERSECT",VERTEX,{"derivedFrom":[subQ0,sQuery(id+"F7.wireOp",EDGE,"E45.2.1")]}),-1.0]])],"derivedFrom":subQ0})])]})]})})]});}
            var Q3;
            {var subQ0=sQuery(id+"F7.wireOp",EDGE,"E39");var subQ1=sQuery(id+"F7.wireOp",EDGE,"E45.5.1");Q3=makeQuery(id+"F10.opFillet","BLEND_EDGE",EDGE,{"blendedFrom":[makeQuery(id+"F8.boolean.opBoolean","INTERSECT",EDGE,{"derivedFrom":[makeQuery(id+"F1.opRevolve","SWEPT_FACE",FACE,{"disambiguationData":[OSD([sQuery(id+"F0.wireOp",EDGE,"E35")])]}),makeQuery(id+"F8.opExtrude","SWEPT_FACE",FACE,{"disambiguationData":[OSD([subQ1])]})]}),makeQuery(id+"F9.opFillet","SPLIT",FACE,{"disambiguationData":[OD(0.0)],"derivedFrom":makeQuery(id+"F8.boolean.opBoolean","MERGE",FACE,{"derivedFrom":[makeQuery(id+"F1.opRevolve","SWEPT_FACE",FACE,{"disambiguationData":[OSD([sQuery(id+"F0.wireOp",EDGE,"E36")])]}),makeQuery(id+"F8.opExtrude","SWEPT_FACE",FACE,{"disambiguationData":[OSD([subQ0]),TDD([makeQuery(id+"F7.imprint","IMPRINT",EDGE,{"disambiguationData":[TD([[makeQuery(id+"F7.imprint","INTERSECT",VERTEX,{"derivedFrom":[subQ0,sQuery(id+"F7.wireOp",EDGE,"E45.3.1")]}),-1.0]])],"derivedFrom":subQ0})])]}),makeQuery(id+"F8.opExtrude","SWEPT_FACE",FACE,{"disambiguationData":[OSD([subQ0]),TDD([makeQuery(id+"F7.imprint","IMPRINT",EDGE,{"disambiguationData":[TD([[makeQuery(id+"F7.imprint","INTERSECT",VERTEX,{"derivedFrom":[subQ0,sQuery(id+"F7.wireOp",EDGE,"E45.4.1")]}),-1.0]])],"derivedFrom":subQ0})])]}),makeQuery(id+"F8.opExtrude","SWEPT_FACE",FACE,{"disambiguationData":[OSD([subQ0]),TDD([makeQuery(id+"F7.imprint","IMPRINT",EDGE,{"disambiguationData":[TD([[makeQuery(id+"F7.imprint","INTERSECT",VERTEX,{"derivedFrom":[subQ0,sQuery(id+"F7.wireOp",EDGE,"E43")]}),1.0]])],"derivedFrom":subQ0})])]}),makeQuery(id+"F8.opExtrude","SWEPT_FACE",FACE,{"disambiguationData":[OSD([subQ0]),TDD([makeQuery(id+"F7.imprint","IMPRINT",EDGE,{"disambiguationData":[TD([[makeQuery(id+"F7.imprint","INTERSECT",VERTEX,{"derivedFrom":[subQ0,sQuery(id+"F7.wireOp",EDGE,"E44")]}),-1.0]])],"derivedFrom":subQ0})])]}),makeQuery(id+"F8.opExtrude","SWEPT_FACE",FACE,{"disambiguationData":[OSD([subQ0]),TDD([makeQuery(id+"F7.imprint","IMPRINT",EDGE,{"disambiguationData":[TD([[makeQuery(id+"F7.imprint","INTERSECT",VERTEX,{"derivedFrom":[subQ0,sQuery(id+"F7.wireOp",EDGE,"E45.1.1")]}),-1.0]])],"derivedFrom":subQ0})])]}),makeQuery(id+"F8.opExtrude","SWEPT_FACE",FACE,{"disambiguationData":[OSD([subQ0]),TDD([makeQuery(id+"F7.imprint","IMPRINT",EDGE,{"disambiguationData":[TD([[makeQuery(id+"F7.imprint","INTERSECT",VERTEX,{"derivedFrom":[subQ0,sQuery(id+"F7.wireOp",EDGE,"E45.2.1")]}),-1.0]])],"derivedFrom":subQ0})])]})]})})],"blendedInto":[makeQuery(id+"F9.opFillet","SPLIT",FACE,{"disambiguationData":[OD(0.0)],"derivedFrom":makeQuery(id+"F8.boolean.opBoolean","MERGE",FACE,{"derivedFrom":[makeQuery(id+"F1.opRevolve","SWEPT_FACE",FACE,{"disambiguationData":[OSD([sQuery(id+"F0.wireOp",EDGE,"E36")])]}),makeQuery(id+"F8.opExtrude","SWEPT_FACE",FACE,{"disambiguationData":[OSD([subQ0]),TDD([makeQuery(id+"F7.imprint","IMPRINT",EDGE,{"disambiguationData":[TD([[makeQuery(id+"F7.imprint","INTERSECT",VERTEX,{"derivedFrom":[subQ0,sQuery(id+"F7.wireOp",EDGE,"E45.3.1")]}),-1.0]])],"derivedFrom":subQ0})])]}),makeQuery(id+"F8.opExtrude","SWEPT_FACE",FACE,{"disambiguationData":[OSD([subQ0]),TDD([makeQuery(id+"F7.imprint","IMPRINT",EDGE,{"disambiguationData":[TD([[makeQuery(id+"F7.imprint","INTERSECT",VERTEX,{"derivedFrom":[subQ0,sQuery(id+"F7.wireOp",EDGE,"E45.4.1")]}),-1.0]])],"derivedFrom":subQ0})])]}),makeQuery(id+"F8.opExtrude","SWEPT_FACE",FACE,{"disambiguationData":[OSD([subQ0]),TDD([makeQuery(id+"F7.imprint","IMPRINT",EDGE,{"disambiguationData":[TD([[makeQuery(id+"F7.imprint","INTERSECT",VERTEX,{"derivedFrom":[subQ0,sQuery(id+"F7.wireOp",EDGE,"E43")]}),1.0]])],"derivedFrom":subQ0})])]}),makeQuery(id+"F8.opExtrude","SWEPT_FACE",FACE,{"disambiguationData":[OSD([subQ0]),TDD([makeQuery(id+"F7.imprint","IMPRINT",EDGE,{"disambiguationData":[TD([[makeQuery(id+"F7.imprint","INTERSECT",VERTEX,{"derivedFrom":[subQ0,sQuery(id+"F7.wireOp",EDGE,"E44")]}),-1.0]])],"derivedFrom":subQ0})])]}),makeQuery(id+"F8.opExtrude","SWEPT_FACE",FACE,{"disambiguationData":[OSD([subQ0]),TDD([makeQuery(id+"F7.imprint","IMPRINT",EDGE,{"disambiguationData":[TD([[makeQuery(id+"F7.imprint","INTERSECT",VERTEX,{"derivedFrom":[subQ0,sQuery(id+"F7.wireOp",EDGE,"E45.1.1")]}),-1.0]])],"derivedFrom":subQ0})])]}),makeQuery(id+"F8.opExtrude","SWEPT_FACE",FACE,{"disambiguationData":[OSD([subQ0]),TDD([makeQuery(id+"F7.imprint","IMPRINT",EDGE,{"disambiguationData":[TD([[makeQuery(id+"F7.imprint","INTERSECT",VERTEX,{"derivedFrom":[subQ0,sQuery(id+"F7.wireOp",EDGE,"E45.2.1")]}),-1.0]])],"derivedFrom":subQ0})])]})]})})]});}
            var Q4;
            {var subQ0=sQuery(id+"F7.wireOp",EDGE,"E40");var subQ1=sQuery(id+"F7.wireOp",EDGE,"E45.4.3");Q4=makeQuery(id+"F10.opFillet","BLEND_EDGE",EDGE,{"blendedFrom":[makeQuery(id+"F8.boolean.opBoolean","INTERSECT",EDGE,{"derivedFrom":[makeQuery(id+"F1.opRevolve","SWEPT_FACE",FACE,{"disambiguationData":[OSD([sQuery(id+"F0.wireOp",EDGE,"E35")])]}),makeQuery(id+"F8.opExtrude","SWEPT_FACE",FACE,{"disambiguationData":[OSD([subQ1])]})]}),makeQuery(id+"F9.opFillet","SPLIT",FACE,{"disambiguationData":[OD(4.0)],"derivedFrom":makeQuery(id+"F8.boolean.opBoolean","MERGE",FACE,{"derivedFrom":[makeQuery(id+"F1.opRevolve","SWEPT_FACE",FACE,{"disambiguationData":[OSD([sQuery(id+"F0.wireOp",EDGE,"E34")])]}),makeQuery(id+"F8.opExtrude","SWEPT_FACE",FACE,{"disambiguationData":[OSD([subQ0]),TDD([makeQuery(id+"F7.imprint","IMPRINT",EDGE,{"disambiguationData":[TD([[makeQuery(id+"F7.imprint","INTERSECT",VERTEX,{"derivedFrom":[subQ0,sQuery(id+"F7.wireOp",EDGE,"E45.3.1")]}),-1.0]])],"derivedFrom":subQ0})])]}),makeQuery(id+"F8.opExtrude","SWEPT_FACE",FACE,{"disambiguationData":[OSD([subQ0]),TDD([makeQuery(id+"F7.imprint","IMPRINT",EDGE,{"disambiguationData":[TD([[makeQuery(id+"F7.imprint","INTERSECT",VERTEX,{"derivedFrom":[subQ0,sQuery(id+"F7.wireOp",EDGE,"E45.4.1")]}),-1.0]])],"derivedFrom":subQ0})])]}),makeQuery(id+"F8.opExtrude","SWEPT_FACE",FACE,{"disambiguationData":[OSD([subQ0]),TDD([makeQuery(id+"F7.imprint","IMPRINT",EDGE,{"disambiguationData":[TD([[makeQuery(id+"F7.imprint","INTERSECT",VERTEX,{"derivedFrom":[subQ0,sQuery(id+"F7.wireOp",EDGE,"E43")]}),1.0]])],"derivedFrom":subQ0})])]}),makeQuery(id+"F8.opExtrude","SWEPT_FACE",FACE,{"disambiguationData":[OSD([subQ0]),TDD([makeQuery(id+"F7.imprint","IMPRINT",EDGE,{"disambiguationData":[TD([[makeQuery(id+"F7.imprint","INTERSECT",VERTEX,{"derivedFrom":[subQ0,sQuery(id+"F7.wireOp",EDGE,"E44")]}),-1.0]])],"derivedFrom":subQ0})])]}),makeQuery(id+"F8.opExtrude","SWEPT_FACE",FACE,{"disambiguationData":[OSD([subQ0]),TDD([makeQuery(id+"F7.imprint","IMPRINT",EDGE,{"disambiguationData":[TD([[makeQuery(id+"F7.imprint","INTERSECT",VERTEX,{"derivedFrom":[subQ0,sQuery(id+"F7.wireOp",EDGE,"E45.1.1")]}),-1.0]])],"derivedFrom":subQ0})])]}),makeQuery(id+"F8.opExtrude","SWEPT_FACE",FACE,{"disambiguationData":[OSD([subQ0]),TDD([makeQuery(id+"F7.imprint","IMPRINT",EDGE,{"disambiguationData":[TD([[makeQuery(id+"F7.imprint","INTERSECT",VERTEX,{"derivedFrom":[subQ0,sQuery(id+"F7.wireOp",EDGE,"E45.2.1")]}),-1.0]])],"derivedFrom":subQ0})])]})]})})],"blendedInto":[makeQuery(id+"F9.opFillet","SPLIT",FACE,{"disambiguationData":[OD(4.0)],"derivedFrom":makeQuery(id+"F8.boolean.opBoolean","MERGE",FACE,{"derivedFrom":[makeQuery(id+"F1.opRevolve","SWEPT_FACE",FACE,{"disambiguationData":[OSD([sQuery(id+"F0.wireOp",EDGE,"E34")])]}),makeQuery(id+"F8.opExtrude","SWEPT_FACE",FACE,{"disambiguationData":[OSD([subQ0]),TDD([makeQuery(id+"F7.imprint","IMPRINT",EDGE,{"disambiguationData":[TD([[makeQuery(id+"F7.imprint","INTERSECT",VERTEX,{"derivedFrom":[subQ0,sQuery(id+"F7.wireOp",EDGE,"E45.3.1")]}),-1.0]])],"derivedFrom":subQ0})])]}),makeQuery(id+"F8.opExtrude","SWEPT_FACE",FACE,{"disambiguationData":[OSD([subQ0]),TDD([makeQuery(id+"F7.imprint","IMPRINT",EDGE,{"disambiguationData":[TD([[makeQuery(id+"F7.imprint","INTERSECT",VERTEX,{"derivedFrom":[subQ0,sQuery(id+"F7.wireOp",EDGE,"E45.4.1")]}),-1.0]])],"derivedFrom":subQ0})])]}),makeQuery(id+"F8.opExtrude","SWEPT_FACE",FACE,{"disambiguationData":[OSD([subQ0]),TDD([makeQuery(id+"F7.imprint","IMPRINT",EDGE,{"disambiguationData":[TD([[makeQuery(id+"F7.imprint","INTERSECT",VERTEX,{"derivedFrom":[subQ0,sQuery(id+"F7.wireOp",EDGE,"E43")]}),1.0]])],"derivedFrom":subQ0})])]}),makeQuery(id+"F8.opExtrude","SWEPT_FACE",FACE,{"disambiguationData":[OSD([subQ0]),TDD([makeQuery(id+"F7.imprint","IMPRINT",EDGE,{"disambiguationData":[TD([[makeQuery(id+"F7.imprint","INTERSECT",VERTEX,{"derivedFrom":[subQ0,sQuery(id+"F7.wireOp",EDGE,"E44")]}),-1.0]])],"derivedFrom":subQ0})])]}),makeQuery(id+"F8.opExtrude","SWEPT_FACE",FACE,{"disambiguationData":[OSD([subQ0]),TDD([makeQuery(id+"F7.imprint","IMPRINT",EDGE,{"disambiguationData":[TD([[makeQuery(id+"F7.imprint","INTERSECT",VERTEX,{"derivedFrom":[subQ0,sQuery(id+"F7.wireOp",EDGE,"E45.1.1")]}),-1.0]])],"derivedFrom":subQ0})])]}),makeQuery(id+"F8.opExtrude","SWEPT_FACE",FACE,{"disambiguationData":[OSD([subQ0]),TDD([makeQuery(id+"F7.imprint","IMPRINT",EDGE,{"disambiguationData":[TD([[makeQuery(id+"F7.imprint","INTERSECT",VERTEX,{"derivedFrom":[subQ0,sQuery(id+"F7.wireOp",EDGE,"E45.2.1")]}),-1.0]])],"derivedFrom":subQ0})])]})]})})]});}
            var Q5;
            {var subQ0=sQuery(id+"F7.wireOp",EDGE,"E39");var subQ1=sQuery(id+"F7.wireOp",EDGE,"E45.4.1");Q5=makeQuery(id+"F10.opFillet","BLEND_EDGE",EDGE,{"blendedFrom":[makeQuery(id+"F8.boolean.opBoolean","INTERSECT",EDGE,{"derivedFrom":[makeQuery(id+"F1.opRevolve","SWEPT_FACE",FACE,{"disambiguationData":[OSD([sQuery(id+"F0.wireOp",EDGE,"E35")])]}),makeQuery(id+"F8.opExtrude","SWEPT_FACE",FACE,{"disambiguationData":[OSD([subQ1])]})]}),makeQuery(id+"F9.opFillet","SPLIT",FACE,{"disambiguationData":[OD(5.0)],"derivedFrom":makeQuery(id+"F8.boolean.opBoolean","MERGE",FACE,{"derivedFrom":[makeQuery(id+"F1.opRevolve","SWEPT_FACE",FACE,{"disambiguationData":[OSD([sQuery(id+"F0.wireOp",EDGE,"E36")])]}),makeQuery(id+"F8.opExtrude","SWEPT_FACE",FACE,{"disambiguationData":[OSD([subQ0]),TDD([makeQuery(id+"F7.imprint","IMPRINT",EDGE,{"disambiguationData":[TD([[makeQuery(id+"F7.imprint","INTERSECT",VERTEX,{"derivedFrom":[subQ0,sQuery(id+"F7.wireOp",EDGE,"E45.3.1")]}),-1.0]])],"derivedFrom":subQ0})])]}),makeQuery(id+"F8.opExtrude","SWEPT_FACE",FACE,{"disambiguationData":[OSD([subQ0]),TDD([makeQuery(id+"F7.imprint","IMPRINT",EDGE,{"disambiguationData":[TD([[makeQuery(id+"F7.imprint","INTERSECT",VERTEX,{"derivedFrom":[subQ0,subQ1]}),-1.0]])],"derivedFrom":subQ0})])]}),makeQuery(id+"F8.opExtrude","SWEPT_FACE",FACE,{"disambiguationData":[OSD([subQ0]),TDD([makeQuery(id+"F7.imprint","IMPRINT",EDGE,{"disambiguationData":[TD([[makeQuery(id+"F7.imprint","INTERSECT",VERTEX,{"derivedFrom":[subQ0,sQuery(id+"F7.wireOp",EDGE,"E43")]}),1.0]])],"derivedFrom":subQ0})])]}),makeQuery(id+"F8.opExtrude","SWEPT_FACE",FACE,{"disambiguationData":[OSD([subQ0]),TDD([makeQuery(id+"F7.imprint","IMPRINT",EDGE,{"disambiguationData":[TD([[makeQuery(id+"F7.imprint","INTERSECT",VERTEX,{"derivedFrom":[subQ0,sQuery(id+"F7.wireOp",EDGE,"E44")]}),-1.0]])],"derivedFrom":subQ0})])]}),makeQuery(id+"F8.opExtrude","SWEPT_FACE",FACE,{"disambiguationData":[OSD([subQ0]),TDD([makeQuery(id+"F7.imprint","IMPRINT",EDGE,{"disambiguationData":[TD([[makeQuery(id+"F7.imprint","INTERSECT",VERTEX,{"derivedFrom":[subQ0,sQuery(id+"F7.wireOp",EDGE,"E45.1.1")]}),-1.0]])],"derivedFrom":subQ0})])]}),makeQuery(id+"F8.opExtrude","SWEPT_FACE",FACE,{"disambiguationData":[OSD([subQ0]),TDD([makeQuery(id+"F7.imprint","IMPRINT",EDGE,{"disambiguationData":[TD([[makeQuery(id+"F7.imprint","INTERSECT",VERTEX,{"derivedFrom":[subQ0,sQuery(id+"F7.wireOp",EDGE,"E45.2.1")]}),-1.0]])],"derivedFrom":subQ0})])]})]})})],"blendedInto":[makeQuery(id+"F9.opFillet","SPLIT",FACE,{"disambiguationData":[OD(5.0)],"derivedFrom":makeQuery(id+"F8.boolean.opBoolean","MERGE",FACE,{"derivedFrom":[makeQuery(id+"F1.opRevolve","SWEPT_FACE",FACE,{"disambiguationData":[OSD([sQuery(id+"F0.wireOp",EDGE,"E36")])]}),makeQuery(id+"F8.opExtrude","SWEPT_FACE",FACE,{"disambiguationData":[OSD([subQ0]),TDD([makeQuery(id+"F7.imprint","IMPRINT",EDGE,{"disambiguationData":[TD([[makeQuery(id+"F7.imprint","INTERSECT",VERTEX,{"derivedFrom":[subQ0,sQuery(id+"F7.wireOp",EDGE,"E45.3.1")]}),-1.0]])],"derivedFrom":subQ0})])]}),makeQuery(id+"F8.opExtrude","SWEPT_FACE",FACE,{"disambiguationData":[OSD([subQ0]),TDD([makeQuery(id+"F7.imprint","IMPRINT",EDGE,{"disambiguationData":[TD([[makeQuery(id+"F7.imprint","INTERSECT",VERTEX,{"derivedFrom":[subQ0,subQ1]}),-1.0]])],"derivedFrom":subQ0})])]}),makeQuery(id+"F8.opExtrude","SWEPT_FACE",FACE,{"disambiguationData":[OSD([subQ0]),TDD([makeQuery(id+"F7.imprint","IMPRINT",EDGE,{"disambiguationData":[TD([[makeQuery(id+"F7.imprint","INTERSECT",VERTEX,{"derivedFrom":[subQ0,sQuery(id+"F7.wireOp",EDGE,"E43")]}),1.0]])],"derivedFrom":subQ0})])]}),makeQuery(id+"F8.opExtrude","SWEPT_FACE",FACE,{"disambiguationData":[OSD([subQ0]),TDD([makeQuery(id+"F7.imprint","IMPRINT",EDGE,{"disambiguationData":[TD([[makeQuery(id+"F7.imprint","INTERSECT",VERTEX,{"derivedFrom":[subQ0,sQuery(id+"F7.wireOp",EDGE,"E44")]}),-1.0]])],"derivedFrom":subQ0})])]}),makeQuery(id+"F8.opExtrude","SWEPT_FACE",FACE,{"disambiguationData":[OSD([subQ0]),TDD([makeQuery(id+"F7.imprint","IMPRINT",EDGE,{"disambiguationData":[TD([[makeQuery(id+"F7.imprint","INTERSECT",VERTEX,{"derivedFrom":[subQ0,sQuery(id+"F7.wireOp",EDGE,"E45.1.1")]}),-1.0]])],"derivedFrom":subQ0})])]}),makeQuery(id+"F8.opExtrude","SWEPT_FACE",FACE,{"disambiguationData":[OSD([subQ0]),TDD([makeQuery(id+"F7.imprint","IMPRINT",EDGE,{"disambiguationData":[TD([[makeQuery(id+"F7.imprint","INTERSECT",VERTEX,{"derivedFrom":[subQ0,sQuery(id+"F7.wireOp",EDGE,"E45.2.1")]}),-1.0]])],"derivedFrom":subQ0})])]})]})})]});}
            var Q6;
            {var subQ0=sQuery(id+"F7.wireOp",EDGE,"E39");var subQ1=sQuery(id+"F7.wireOp",EDGE,"E45.3.3");Q6=makeQuery(id+"F10.opFillet","BLEND_EDGE",EDGE,{"blendedFrom":[makeQuery(id+"F8.boolean.opBoolean","INTERSECT",EDGE,{"derivedFrom":[makeQuery(id+"F1.opRevolve","SWEPT_FACE",FACE,{"disambiguationData":[OSD([sQuery(id+"F0.wireOp",EDGE,"E35")])]}),makeQuery(id+"F8.opExtrude","SWEPT_FACE",FACE,{"disambiguationData":[OSD([subQ1])]})]}),makeQuery(id+"F9.opFillet","SPLIT",FACE,{"disambiguationData":[OD(3.0)],"derivedFrom":makeQuery(id+"F8.boolean.opBoolean","MERGE",FACE,{"derivedFrom":[makeQuery(id+"F1.opRevolve","SWEPT_FACE",FACE,{"disambiguationData":[OSD([sQuery(id+"F0.wireOp",EDGE,"E36")])]}),makeQuery(id+"F8.opExtrude","SWEPT_FACE",FACE,{"disambiguationData":[OSD([subQ0]),TDD([makeQuery(id+"F7.imprint","IMPRINT",EDGE,{"disambiguationData":[TD([[makeQuery(id+"F7.imprint","INTERSECT",VERTEX,{"derivedFrom":[subQ0,sQuery(id+"F7.wireOp",EDGE,"E45.3.1")]}),-1.0]])],"derivedFrom":subQ0})])]}),makeQuery(id+"F8.opExtrude","SWEPT_FACE",FACE,{"disambiguationData":[OSD([subQ0]),TDD([makeQuery(id+"F7.imprint","IMPRINT",EDGE,{"disambiguationData":[TD([[makeQuery(id+"F7.imprint","INTERSECT",VERTEX,{"derivedFrom":[subQ0,sQuery(id+"F7.wireOp",EDGE,"E45.4.1")]}),-1.0]])],"derivedFrom":subQ0})])]}),makeQuery(id+"F8.opExtrude","SWEPT_FACE",FACE,{"disambiguationData":[OSD([subQ0]),TDD([makeQuery(id+"F7.imprint","IMPRINT",EDGE,{"disambiguationData":[TD([[makeQuery(id+"F7.imprint","INTERSECT",VERTEX,{"derivedFrom":[subQ0,sQuery(id+"F7.wireOp",EDGE,"E43")]}),1.0]])],"derivedFrom":subQ0})])]}),makeQuery(id+"F8.opExtrude","SWEPT_FACE",FACE,{"disambiguationData":[OSD([subQ0]),TDD([makeQuery(id+"F7.imprint","IMPRINT",EDGE,{"disambiguationData":[TD([[makeQuery(id+"F7.imprint","INTERSECT",VERTEX,{"derivedFrom":[subQ0,sQuery(id+"F7.wireOp",EDGE,"E44")]}),-1.0]])],"derivedFrom":subQ0})])]}),makeQuery(id+"F8.opExtrude","SWEPT_FACE",FACE,{"disambiguationData":[OSD([subQ0]),TDD([makeQuery(id+"F7.imprint","IMPRINT",EDGE,{"disambiguationData":[TD([[makeQuery(id+"F7.imprint","INTERSECT",VERTEX,{"derivedFrom":[subQ0,sQuery(id+"F7.wireOp",EDGE,"E45.1.1")]}),-1.0]])],"derivedFrom":subQ0})])]}),makeQuery(id+"F8.opExtrude","SWEPT_FACE",FACE,{"disambiguationData":[OSD([subQ0]),TDD([makeQuery(id+"F7.imprint","IMPRINT",EDGE,{"disambiguationData":[TD([[makeQuery(id+"F7.imprint","INTERSECT",VERTEX,{"derivedFrom":[subQ0,sQuery(id+"F7.wireOp",EDGE,"E45.2.1")]}),-1.0]])],"derivedFrom":subQ0})])]})]})})],"blendedInto":[makeQuery(id+"F9.opFillet","SPLIT",FACE,{"disambiguationData":[OD(3.0)],"derivedFrom":makeQuery(id+"F8.boolean.opBoolean","MERGE",FACE,{"derivedFrom":[makeQuery(id+"F1.opRevolve","SWEPT_FACE",FACE,{"disambiguationData":[OSD([sQuery(id+"F0.wireOp",EDGE,"E36")])]}),makeQuery(id+"F8.opExtrude","SWEPT_FACE",FACE,{"disambiguationData":[OSD([subQ0]),TDD([makeQuery(id+"F7.imprint","IMPRINT",EDGE,{"disambiguationData":[TD([[makeQuery(id+"F7.imprint","INTERSECT",VERTEX,{"derivedFrom":[subQ0,sQuery(id+"F7.wireOp",EDGE,"E45.3.1")]}),-1.0]])],"derivedFrom":subQ0})])]}),makeQuery(id+"F8.opExtrude","SWEPT_FACE",FACE,{"disambiguationData":[OSD([subQ0]),TDD([makeQuery(id+"F7.imprint","IMPRINT",EDGE,{"disambiguationData":[TD([[makeQuery(id+"F7.imprint","INTERSECT",VERTEX,{"derivedFrom":[subQ0,sQuery(id+"F7.wireOp",EDGE,"E45.4.1")]}),-1.0]])],"derivedFrom":subQ0})])]}),makeQuery(id+"F8.opExtrude","SWEPT_FACE",FACE,{"disambiguationData":[OSD([subQ0]),TDD([makeQuery(id+"F7.imprint","IMPRINT",EDGE,{"disambiguationData":[TD([[makeQuery(id+"F7.imprint","INTERSECT",VERTEX,{"derivedFrom":[subQ0,sQuery(id+"F7.wireOp",EDGE,"E43")]}),1.0]])],"derivedFrom":subQ0})])]}),makeQuery(id+"F8.opExtrude","SWEPT_FACE",FACE,{"disambiguationData":[OSD([subQ0]),TDD([makeQuery(id+"F7.imprint","IMPRINT",EDGE,{"disambiguationData":[TD([[makeQuery(id+"F7.imprint","INTERSECT",VERTEX,{"derivedFrom":[subQ0,sQuery(id+"F7.wireOp",EDGE,"E44")]}),-1.0]])],"derivedFrom":subQ0})])]}),makeQuery(id+"F8.opExtrude","SWEPT_FACE",FACE,{"disambiguationData":[OSD([subQ0]),TDD([makeQuery(id+"F7.imprint","IMPRINT",EDGE,{"disambiguationData":[TD([[makeQuery(id+"F7.imprint","INTERSECT",VERTEX,{"derivedFrom":[subQ0,sQuery(id+"F7.wireOp",EDGE,"E45.1.1")]}),-1.0]])],"derivedFrom":subQ0})])]}),makeQuery(id+"F8.opExtrude","SWEPT_FACE",FACE,{"disambiguationData":[OSD([subQ0]),TDD([makeQuery(id+"F7.imprint","IMPRINT",EDGE,{"disambiguationData":[TD([[makeQuery(id+"F7.imprint","INTERSECT",VERTEX,{"derivedFrom":[subQ0,sQuery(id+"F7.wireOp",EDGE,"E45.2.1")]}),-1.0]])],"derivedFrom":subQ0})])]})]})})]});}
            var Q7;
            {var subQ0=sQuery(id+"F7.wireOp",EDGE,"E40");var subQ1=sQuery(id+"F7.wireOp",EDGE,"E45.3.1");Q7=makeQuery(id+"F10.opFillet","BLEND_EDGE",EDGE,{"blendedFrom":[makeQuery(id+"F8.boolean.opBoolean","INTERSECT",EDGE,{"derivedFrom":[makeQuery(id+"F1.opRevolve","SWEPT_FACE",FACE,{"disambiguationData":[OSD([sQuery(id+"F0.wireOp",EDGE,"E35")])]}),makeQuery(id+"F8.opExtrude","SWEPT_FACE",FACE,{"disambiguationData":[OSD([subQ1])]})]}),makeQuery(id+"F9.opFillet","SPLIT",FACE,{"disambiguationData":[OD(4.0)],"derivedFrom":makeQuery(id+"F8.boolean.opBoolean","MERGE",FACE,{"derivedFrom":[makeQuery(id+"F1.opRevolve","SWEPT_FACE",FACE,{"disambiguationData":[OSD([sQuery(id+"F0.wireOp",EDGE,"E34")])]}),makeQuery(id+"F8.opExtrude","SWEPT_FACE",FACE,{"disambiguationData":[OSD([subQ0]),TDD([makeQuery(id+"F7.imprint","IMPRINT",EDGE,{"disambiguationData":[TD([[makeQuery(id+"F7.imprint","INTERSECT",VERTEX,{"derivedFrom":[subQ0,subQ1]}),-1.0]])],"derivedFrom":subQ0})])]}),makeQuery(id+"F8.opExtrude","SWEPT_FACE",FACE,{"disambiguationData":[OSD([subQ0]),TDD([makeQuery(id+"F7.imprint","IMPRINT",EDGE,{"disambiguationData":[TD([[makeQuery(id+"F7.imprint","INTERSECT",VERTEX,{"derivedFrom":[subQ0,sQuery(id+"F7.wireOp",EDGE,"E45.4.1")]}),-1.0]])],"derivedFrom":subQ0})])]}),makeQuery(id+"F8.opExtrude","SWEPT_FACE",FACE,{"disambiguationData":[OSD([subQ0]),TDD([makeQuery(id+"F7.imprint","IMPRINT",EDGE,{"disambiguationData":[TD([[makeQuery(id+"F7.imprint","INTERSECT",VERTEX,{"derivedFrom":[subQ0,sQuery(id+"F7.wireOp",EDGE,"E43")]}),1.0]])],"derivedFrom":subQ0})])]}),makeQuery(id+"F8.opExtrude","SWEPT_FACE",FACE,{"disambiguationData":[OSD([subQ0]),TDD([makeQuery(id+"F7.imprint","IMPRINT",EDGE,{"disambiguationData":[TD([[makeQuery(id+"F7.imprint","INTERSECT",VERTEX,{"derivedFrom":[subQ0,sQuery(id+"F7.wireOp",EDGE,"E44")]}),-1.0]])],"derivedFrom":subQ0})])]}),makeQuery(id+"F8.opExtrude","SWEPT_FACE",FACE,{"disambiguationData":[OSD([subQ0]),TDD([makeQuery(id+"F7.imprint","IMPRINT",EDGE,{"disambiguationData":[TD([[makeQuery(id+"F7.imprint","INTERSECT",VERTEX,{"derivedFrom":[subQ0,sQuery(id+"F7.wireOp",EDGE,"E45.1.1")]}),-1.0]])],"derivedFrom":subQ0})])]}),makeQuery(id+"F8.opExtrude","SWEPT_FACE",FACE,{"disambiguationData":[OSD([subQ0]),TDD([makeQuery(id+"F7.imprint","IMPRINT",EDGE,{"disambiguationData":[TD([[makeQuery(id+"F7.imprint","INTERSECT",VERTEX,{"derivedFrom":[subQ0,sQuery(id+"F7.wireOp",EDGE,"E45.2.1")]}),-1.0]])],"derivedFrom":subQ0})])]})]})})],"blendedInto":[makeQuery(id+"F9.opFillet","SPLIT",FACE,{"disambiguationData":[OD(4.0)],"derivedFrom":makeQuery(id+"F8.boolean.opBoolean","MERGE",FACE,{"derivedFrom":[makeQuery(id+"F1.opRevolve","SWEPT_FACE",FACE,{"disambiguationData":[OSD([sQuery(id+"F0.wireOp",EDGE,"E34")])]}),makeQuery(id+"F8.opExtrude","SWEPT_FACE",FACE,{"disambiguationData":[OSD([subQ0]),TDD([makeQuery(id+"F7.imprint","IMPRINT",EDGE,{"disambiguationData":[TD([[makeQuery(id+"F7.imprint","INTERSECT",VERTEX,{"derivedFrom":[subQ0,subQ1]}),-1.0]])],"derivedFrom":subQ0})])]}),makeQuery(id+"F8.opExtrude","SWEPT_FACE",FACE,{"disambiguationData":[OSD([subQ0]),TDD([makeQuery(id+"F7.imprint","IMPRINT",EDGE,{"disambiguationData":[TD([[makeQuery(id+"F7.imprint","INTERSECT",VERTEX,{"derivedFrom":[subQ0,sQuery(id+"F7.wireOp",EDGE,"E45.4.1")]}),-1.0]])],"derivedFrom":subQ0})])]}),makeQuery(id+"F8.opExtrude","SWEPT_FACE",FACE,{"disambiguationData":[OSD([subQ0]),TDD([makeQuery(id+"F7.imprint","IMPRINT",EDGE,{"disambiguationData":[TD([[makeQuery(id+"F7.imprint","INTERSECT",VERTEX,{"derivedFrom":[subQ0,sQuery(id+"F7.wireOp",EDGE,"E43")]}),1.0]])],"derivedFrom":subQ0})])]}),makeQuery(id+"F8.opExtrude","SWEPT_FACE",FACE,{"disambiguationData":[OSD([subQ0]),TDD([makeQuery(id+"F7.imprint","IMPRINT",EDGE,{"disambiguationData":[TD([[makeQuery(id+"F7.imprint","INTERSECT",VERTEX,{"derivedFrom":[subQ0,sQuery(id+"F7.wireOp",EDGE,"E44")]}),-1.0]])],"derivedFrom":subQ0})])]}),makeQuery(id+"F8.opExtrude","SWEPT_FACE",FACE,{"disambiguationData":[OSD([subQ0]),TDD([makeQuery(id+"F7.imprint","IMPRINT",EDGE,{"disambiguationData":[TD([[makeQuery(id+"F7.imprint","INTERSECT",VERTEX,{"derivedFrom":[subQ0,sQuery(id+"F7.wireOp",EDGE,"E45.1.1")]}),-1.0]])],"derivedFrom":subQ0})])]}),makeQuery(id+"F8.opExtrude","SWEPT_FACE",FACE,{"disambiguationData":[OSD([subQ0]),TDD([makeQuery(id+"F7.imprint","IMPRINT",EDGE,{"disambiguationData":[TD([[makeQuery(id+"F7.imprint","INTERSECT",VERTEX,{"derivedFrom":[subQ0,sQuery(id+"F7.wireOp",EDGE,"E45.2.1")]}),-1.0]])],"derivedFrom":subQ0})])]})]})})]});}
            var Q8;
            {var subQ0=sQuery(id+"F7.wireOp",EDGE,"E39");var subQ1=sQuery(id+"F7.wireOp",EDGE,"E45.2.3");Q8=makeQuery(id+"F10.opFillet","BLEND_EDGE",EDGE,{"blendedFrom":[makeQuery(id+"F8.boolean.opBoolean","INTERSECT",EDGE,{"derivedFrom":[makeQuery(id+"F1.opRevolve","SWEPT_FACE",FACE,{"disambiguationData":[OSD([sQuery(id+"F0.wireOp",EDGE,"E35")])]}),makeQuery(id+"F8.opExtrude","SWEPT_FACE",FACE,{"disambiguationData":[OSD([subQ1])]})]}),makeQuery(id+"F9.opFillet","SPLIT",FACE,{"disambiguationData":[OD(2.0)],"derivedFrom":makeQuery(id+"F8.boolean.opBoolean","MERGE",FACE,{"derivedFrom":[makeQuery(id+"F1.opRevolve","SWEPT_FACE",FACE,{"disambiguationData":[OSD([sQuery(id+"F0.wireOp",EDGE,"E36")])]}),makeQuery(id+"F8.opExtrude","SWEPT_FACE",FACE,{"disambiguationData":[OSD([subQ0]),TDD([makeQuery(id+"F7.imprint","IMPRINT",EDGE,{"disambiguationData":[TD([[makeQuery(id+"F7.imprint","INTERSECT",VERTEX,{"derivedFrom":[subQ0,sQuery(id+"F7.wireOp",EDGE,"E45.3.1")]}),-1.0]])],"derivedFrom":subQ0})])]}),makeQuery(id+"F8.opExtrude","SWEPT_FACE",FACE,{"disambiguationData":[OSD([subQ0]),TDD([makeQuery(id+"F7.imprint","IMPRINT",EDGE,{"disambiguationData":[TD([[makeQuery(id+"F7.imprint","INTERSECT",VERTEX,{"derivedFrom":[subQ0,sQuery(id+"F7.wireOp",EDGE,"E45.4.1")]}),-1.0]])],"derivedFrom":subQ0})])]}),makeQuery(id+"F8.opExtrude","SWEPT_FACE",FACE,{"disambiguationData":[OSD([subQ0]),TDD([makeQuery(id+"F7.imprint","IMPRINT",EDGE,{"disambiguationData":[TD([[makeQuery(id+"F7.imprint","INTERSECT",VERTEX,{"derivedFrom":[subQ0,sQuery(id+"F7.wireOp",EDGE,"E43")]}),1.0]])],"derivedFrom":subQ0})])]}),makeQuery(id+"F8.opExtrude","SWEPT_FACE",FACE,{"disambiguationData":[OSD([subQ0]),TDD([makeQuery(id+"F7.imprint","IMPRINT",EDGE,{"disambiguationData":[TD([[makeQuery(id+"F7.imprint","INTERSECT",VERTEX,{"derivedFrom":[subQ0,sQuery(id+"F7.wireOp",EDGE,"E44")]}),-1.0]])],"derivedFrom":subQ0})])]}),makeQuery(id+"F8.opExtrude","SWEPT_FACE",FACE,{"disambiguationData":[OSD([subQ0]),TDD([makeQuery(id+"F7.imprint","IMPRINT",EDGE,{"disambiguationData":[TD([[makeQuery(id+"F7.imprint","INTERSECT",VERTEX,{"derivedFrom":[subQ0,sQuery(id+"F7.wireOp",EDGE,"E45.1.1")]}),-1.0]])],"derivedFrom":subQ0})])]}),makeQuery(id+"F8.opExtrude","SWEPT_FACE",FACE,{"disambiguationData":[OSD([subQ0]),TDD([makeQuery(id+"F7.imprint","IMPRINT",EDGE,{"disambiguationData":[TD([[makeQuery(id+"F7.imprint","INTERSECT",VERTEX,{"derivedFrom":[subQ0,sQuery(id+"F7.wireOp",EDGE,"E45.2.1")]}),-1.0]])],"derivedFrom":subQ0})])]})]})})],"blendedInto":[makeQuery(id+"F9.opFillet","SPLIT",FACE,{"disambiguationData":[OD(2.0)],"derivedFrom":makeQuery(id+"F8.boolean.opBoolean","MERGE",FACE,{"derivedFrom":[makeQuery(id+"F1.opRevolve","SWEPT_FACE",FACE,{"disambiguationData":[OSD([sQuery(id+"F0.wireOp",EDGE,"E36")])]}),makeQuery(id+"F8.opExtrude","SWEPT_FACE",FACE,{"disambiguationData":[OSD([subQ0]),TDD([makeQuery(id+"F7.imprint","IMPRINT",EDGE,{"disambiguationData":[TD([[makeQuery(id+"F7.imprint","INTERSECT",VERTEX,{"derivedFrom":[subQ0,sQuery(id+"F7.wireOp",EDGE,"E45.3.1")]}),-1.0]])],"derivedFrom":subQ0})])]}),makeQuery(id+"F8.opExtrude","SWEPT_FACE",FACE,{"disambiguationData":[OSD([subQ0]),TDD([makeQuery(id+"F7.imprint","IMPRINT",EDGE,{"disambiguationData":[TD([[makeQuery(id+"F7.imprint","INTERSECT",VERTEX,{"derivedFrom":[subQ0,sQuery(id+"F7.wireOp",EDGE,"E45.4.1")]}),-1.0]])],"derivedFrom":subQ0})])]}),makeQuery(id+"F8.opExtrude","SWEPT_FACE",FACE,{"disambiguationData":[OSD([subQ0]),TDD([makeQuery(id+"F7.imprint","IMPRINT",EDGE,{"disambiguationData":[TD([[makeQuery(id+"F7.imprint","INTERSECT",VERTEX,{"derivedFrom":[subQ0,sQuery(id+"F7.wireOp",EDGE,"E43")]}),1.0]])],"derivedFrom":subQ0})])]}),makeQuery(id+"F8.opExtrude","SWEPT_FACE",FACE,{"disambiguationData":[OSD([subQ0]),TDD([makeQuery(id+"F7.imprint","IMPRINT",EDGE,{"disambiguationData":[TD([[makeQuery(id+"F7.imprint","INTERSECT",VERTEX,{"derivedFrom":[subQ0,sQuery(id+"F7.wireOp",EDGE,"E44")]}),-1.0]])],"derivedFrom":subQ0})])]}),makeQuery(id+"F8.opExtrude","SWEPT_FACE",FACE,{"disambiguationData":[OSD([subQ0]),TDD([makeQuery(id+"F7.imprint","IMPRINT",EDGE,{"disambiguationData":[TD([[makeQuery(id+"F7.imprint","INTERSECT",VERTEX,{"derivedFrom":[subQ0,sQuery(id+"F7.wireOp",EDGE,"E45.1.1")]}),-1.0]])],"derivedFrom":subQ0})])]}),makeQuery(id+"F8.opExtrude","SWEPT_FACE",FACE,{"disambiguationData":[OSD([subQ0]),TDD([makeQuery(id+"F7.imprint","IMPRINT",EDGE,{"disambiguationData":[TD([[makeQuery(id+"F7.imprint","INTERSECT",VERTEX,{"derivedFrom":[subQ0,sQuery(id+"F7.wireOp",EDGE,"E45.2.1")]}),-1.0]])],"derivedFrom":subQ0})])]})]})})]});}
            var Q9;
            {var subQ0=sQuery(id+"F7.wireOp",EDGE,"E40");var subQ1=sQuery(id+"F7.wireOp",EDGE,"E45.2.3");Q9=makeQuery(id+"F10.opFillet","BLEND_EDGE",EDGE,{"blendedFrom":[makeQuery(id+"F8.boolean.opBoolean","INTERSECT",EDGE,{"derivedFrom":[makeQuery(id+"F1.opRevolve","SWEPT_FACE",FACE,{"disambiguationData":[OSD([sQuery(id+"F0.wireOp",EDGE,"E35")])]}),makeQuery(id+"F8.opExtrude","SWEPT_FACE",FACE,{"disambiguationData":[OSD([subQ1])]})]}),makeQuery(id+"F9.opFillet","SPLIT",FACE,{"disambiguationData":[OD(2.0)],"derivedFrom":makeQuery(id+"F8.boolean.opBoolean","MERGE",FACE,{"derivedFrom":[makeQuery(id+"F1.opRevolve","SWEPT_FACE",FACE,{"disambiguationData":[OSD([sQuery(id+"F0.wireOp",EDGE,"E34")])]}),makeQuery(id+"F8.opExtrude","SWEPT_FACE",FACE,{"disambiguationData":[OSD([subQ0]),TDD([makeQuery(id+"F7.imprint","IMPRINT",EDGE,{"disambiguationData":[TD([[makeQuery(id+"F7.imprint","INTERSECT",VERTEX,{"derivedFrom":[subQ0,sQuery(id+"F7.wireOp",EDGE,"E45.3.1")]}),-1.0]])],"derivedFrom":subQ0})])]}),makeQuery(id+"F8.opExtrude","SWEPT_FACE",FACE,{"disambiguationData":[OSD([subQ0]),TDD([makeQuery(id+"F7.imprint","IMPRINT",EDGE,{"disambiguationData":[TD([[makeQuery(id+"F7.imprint","INTERSECT",VERTEX,{"derivedFrom":[subQ0,sQuery(id+"F7.wireOp",EDGE,"E45.4.1")]}),-1.0]])],"derivedFrom":subQ0})])]}),makeQuery(id+"F8.opExtrude","SWEPT_FACE",FACE,{"disambiguationData":[OSD([subQ0]),TDD([makeQuery(id+"F7.imprint","IMPRINT",EDGE,{"disambiguationData":[TD([[makeQuery(id+"F7.imprint","INTERSECT",VERTEX,{"derivedFrom":[subQ0,sQuery(id+"F7.wireOp",EDGE,"E43")]}),1.0]])],"derivedFrom":subQ0})])]}),makeQuery(id+"F8.opExtrude","SWEPT_FACE",FACE,{"disambiguationData":[OSD([subQ0]),TDD([makeQuery(id+"F7.imprint","IMPRINT",EDGE,{"disambiguationData":[TD([[makeQuery(id+"F7.imprint","INTERSECT",VERTEX,{"derivedFrom":[subQ0,sQuery(id+"F7.wireOp",EDGE,"E44")]}),-1.0]])],"derivedFrom":subQ0})])]}),makeQuery(id+"F8.opExtrude","SWEPT_FACE",FACE,{"disambiguationData":[OSD([subQ0]),TDD([makeQuery(id+"F7.imprint","IMPRINT",EDGE,{"disambiguationData":[TD([[makeQuery(id+"F7.imprint","INTERSECT",VERTEX,{"derivedFrom":[subQ0,sQuery(id+"F7.wireOp",EDGE,"E45.1.1")]}),-1.0]])],"derivedFrom":subQ0})])]}),makeQuery(id+"F8.opExtrude","SWEPT_FACE",FACE,{"disambiguationData":[OSD([subQ0]),TDD([makeQuery(id+"F7.imprint","IMPRINT",EDGE,{"disambiguationData":[TD([[makeQuery(id+"F7.imprint","INTERSECT",VERTEX,{"derivedFrom":[subQ0,sQuery(id+"F7.wireOp",EDGE,"E45.2.1")]}),-1.0]])],"derivedFrom":subQ0})])]})]})})],"blendedInto":[makeQuery(id+"F9.opFillet","SPLIT",FACE,{"disambiguationData":[OD(2.0)],"derivedFrom":makeQuery(id+"F8.boolean.opBoolean","MERGE",FACE,{"derivedFrom":[makeQuery(id+"F1.opRevolve","SWEPT_FACE",FACE,{"disambiguationData":[OSD([sQuery(id+"F0.wireOp",EDGE,"E34")])]}),makeQuery(id+"F8.opExtrude","SWEPT_FACE",FACE,{"disambiguationData":[OSD([subQ0]),TDD([makeQuery(id+"F7.imprint","IMPRINT",EDGE,{"disambiguationData":[TD([[makeQuery(id+"F7.imprint","INTERSECT",VERTEX,{"derivedFrom":[subQ0,sQuery(id+"F7.wireOp",EDGE,"E45.3.1")]}),-1.0]])],"derivedFrom":subQ0})])]}),makeQuery(id+"F8.opExtrude","SWEPT_FACE",FACE,{"disambiguationData":[OSD([subQ0]),TDD([makeQuery(id+"F7.imprint","IMPRINT",EDGE,{"disambiguationData":[TD([[makeQuery(id+"F7.imprint","INTERSECT",VERTEX,{"derivedFrom":[subQ0,sQuery(id+"F7.wireOp",EDGE,"E45.4.1")]}),-1.0]])],"derivedFrom":subQ0})])]}),makeQuery(id+"F8.opExtrude","SWEPT_FACE",FACE,{"disambiguationData":[OSD([subQ0]),TDD([makeQuery(id+"F7.imprint","IMPRINT",EDGE,{"disambiguationData":[TD([[makeQuery(id+"F7.imprint","INTERSECT",VERTEX,{"derivedFrom":[subQ0,sQuery(id+"F7.wireOp",EDGE,"E43")]}),1.0]])],"derivedFrom":subQ0})])]}),makeQuery(id+"F8.opExtrude","SWEPT_FACE",FACE,{"disambiguationData":[OSD([subQ0]),TDD([makeQuery(id+"F7.imprint","IMPRINT",EDGE,{"disambiguationData":[TD([[makeQuery(id+"F7.imprint","INTERSECT",VERTEX,{"derivedFrom":[subQ0,sQuery(id+"F7.wireOp",EDGE,"E44")]}),-1.0]])],"derivedFrom":subQ0})])]}),makeQuery(id+"F8.opExtrude","SWEPT_FACE",FACE,{"disambiguationData":[OSD([subQ0]),TDD([makeQuery(id+"F7.imprint","IMPRINT",EDGE,{"disambiguationData":[TD([[makeQuery(id+"F7.imprint","INTERSECT",VERTEX,{"derivedFrom":[subQ0,sQuery(id+"F7.wireOp",EDGE,"E45.1.1")]}),-1.0]])],"derivedFrom":subQ0})])]}),makeQuery(id+"F8.opExtrude","SWEPT_FACE",FACE,{"disambiguationData":[OSD([subQ0]),TDD([makeQuery(id+"F7.imprint","IMPRINT",EDGE,{"disambiguationData":[TD([[makeQuery(id+"F7.imprint","INTERSECT",VERTEX,{"derivedFrom":[subQ0,sQuery(id+"F7.wireOp",EDGE,"E45.2.1")]}),-1.0]])],"derivedFrom":subQ0})])]})]})})]});}
            var Q10;
            {var subQ0=sQuery(id+"F7.wireOp",EDGE,"E40");var subQ1=sQuery(id+"F7.wireOp",EDGE,"E45.1.1");Q10=makeQuery(id+"F10.opFillet","BLEND_EDGE",EDGE,{"blendedFrom":[makeQuery(id+"F8.boolean.opBoolean","INTERSECT",EDGE,{"derivedFrom":[makeQuery(id+"F1.opRevolve","SWEPT_FACE",FACE,{"disambiguationData":[OSD([sQuery(id+"F0.wireOp",EDGE,"E35")])]}),makeQuery(id+"F8.opExtrude","SWEPT_FACE",FACE,{"disambiguationData":[OSD([subQ1])]})]}),makeQuery(id+"F9.opFillet","SPLIT",FACE,{"disambiguationData":[OD(2.0)],"derivedFrom":makeQuery(id+"F8.boolean.opBoolean","MERGE",FACE,{"derivedFrom":[makeQuery(id+"F1.opRevolve","SWEPT_FACE",FACE,{"disambiguationData":[OSD([sQuery(id+"F0.wireOp",EDGE,"E34")])]}),makeQuery(id+"F8.opExtrude","SWEPT_FACE",FACE,{"disambiguationData":[OSD([subQ0]),TDD([makeQuery(id+"F7.imprint","IMPRINT",EDGE,{"disambiguationData":[TD([[makeQuery(id+"F7.imprint","INTERSECT",VERTEX,{"derivedFrom":[subQ0,sQuery(id+"F7.wireOp",EDGE,"E45.3.1")]}),-1.0]])],"derivedFrom":subQ0})])]}),makeQuery(id+"F8.opExtrude","SWEPT_FACE",FACE,{"disambiguationData":[OSD([subQ0]),TDD([makeQuery(id+"F7.imprint","IMPRINT",EDGE,{"disambiguationData":[TD([[makeQuery(id+"F7.imprint","INTERSECT",VERTEX,{"derivedFrom":[subQ0,sQuery(id+"F7.wireOp",EDGE,"E45.4.1")]}),-1.0]])],"derivedFrom":subQ0})])]}),makeQuery(id+"F8.opExtrude","SWEPT_FACE",FACE,{"disambiguationData":[OSD([subQ0]),TDD([makeQuery(id+"F7.imprint","IMPRINT",EDGE,{"disambiguationData":[TD([[makeQuery(id+"F7.imprint","INTERSECT",VERTEX,{"derivedFrom":[subQ0,sQuery(id+"F7.wireOp",EDGE,"E43")]}),1.0]])],"derivedFrom":subQ0})])]}),makeQuery(id+"F8.opExtrude","SWEPT_FACE",FACE,{"disambiguationData":[OSD([subQ0]),TDD([makeQuery(id+"F7.imprint","IMPRINT",EDGE,{"disambiguationData":[TD([[makeQuery(id+"F7.imprint","INTERSECT",VERTEX,{"derivedFrom":[subQ0,sQuery(id+"F7.wireOp",EDGE,"E44")]}),-1.0]])],"derivedFrom":subQ0})])]}),makeQuery(id+"F8.opExtrude","SWEPT_FACE",FACE,{"disambiguationData":[OSD([subQ0]),TDD([makeQuery(id+"F7.imprint","IMPRINT",EDGE,{"disambiguationData":[TD([[makeQuery(id+"F7.imprint","INTERSECT",VERTEX,{"derivedFrom":[subQ0,subQ1]}),-1.0]])],"derivedFrom":subQ0})])]}),makeQuery(id+"F8.opExtrude","SWEPT_FACE",FACE,{"disambiguationData":[OSD([subQ0]),TDD([makeQuery(id+"F7.imprint","IMPRINT",EDGE,{"disambiguationData":[TD([[makeQuery(id+"F7.imprint","INTERSECT",VERTEX,{"derivedFrom":[subQ0,sQuery(id+"F7.wireOp",EDGE,"E45.2.1")]}),-1.0]])],"derivedFrom":subQ0})])]})]})})],"blendedInto":[makeQuery(id+"F9.opFillet","SPLIT",FACE,{"disambiguationData":[OD(2.0)],"derivedFrom":makeQuery(id+"F8.boolean.opBoolean","MERGE",FACE,{"derivedFrom":[makeQuery(id+"F1.opRevolve","SWEPT_FACE",FACE,{"disambiguationData":[OSD([sQuery(id+"F0.wireOp",EDGE,"E34")])]}),makeQuery(id+"F8.opExtrude","SWEPT_FACE",FACE,{"disambiguationData":[OSD([subQ0]),TDD([makeQuery(id+"F7.imprint","IMPRINT",EDGE,{"disambiguationData":[TD([[makeQuery(id+"F7.imprint","INTERSECT",VERTEX,{"derivedFrom":[subQ0,sQuery(id+"F7.wireOp",EDGE,"E45.3.1")]}),-1.0]])],"derivedFrom":subQ0})])]}),makeQuery(id+"F8.opExtrude","SWEPT_FACE",FACE,{"disambiguationData":[OSD([subQ0]),TDD([makeQuery(id+"F7.imprint","IMPRINT",EDGE,{"disambiguationData":[TD([[makeQuery(id+"F7.imprint","INTERSECT",VERTEX,{"derivedFrom":[subQ0,sQuery(id+"F7.wireOp",EDGE,"E45.4.1")]}),-1.0]])],"derivedFrom":subQ0})])]}),makeQuery(id+"F8.opExtrude","SWEPT_FACE",FACE,{"disambiguationData":[OSD([subQ0]),TDD([makeQuery(id+"F7.imprint","IMPRINT",EDGE,{"disambiguationData":[TD([[makeQuery(id+"F7.imprint","INTERSECT",VERTEX,{"derivedFrom":[subQ0,sQuery(id+"F7.wireOp",EDGE,"E43")]}),1.0]])],"derivedFrom":subQ0})])]}),makeQuery(id+"F8.opExtrude","SWEPT_FACE",FACE,{"disambiguationData":[OSD([subQ0]),TDD([makeQuery(id+"F7.imprint","IMPRINT",EDGE,{"disambiguationData":[TD([[makeQuery(id+"F7.imprint","INTERSECT",VERTEX,{"derivedFrom":[subQ0,sQuery(id+"F7.wireOp",EDGE,"E44")]}),-1.0]])],"derivedFrom":subQ0})])]}),makeQuery(id+"F8.opExtrude","SWEPT_FACE",FACE,{"disambiguationData":[OSD([subQ0]),TDD([makeQuery(id+"F7.imprint","IMPRINT",EDGE,{"disambiguationData":[TD([[makeQuery(id+"F7.imprint","INTERSECT",VERTEX,{"derivedFrom":[subQ0,subQ1]}),-1.0]])],"derivedFrom":subQ0})])]}),makeQuery(id+"F8.opExtrude","SWEPT_FACE",FACE,{"disambiguationData":[OSD([subQ0]),TDD([makeQuery(id+"F7.imprint","IMPRINT",EDGE,{"disambiguationData":[TD([[makeQuery(id+"F7.imprint","INTERSECT",VERTEX,{"derivedFrom":[subQ0,sQuery(id+"F7.wireOp",EDGE,"E45.2.1")]}),-1.0]])],"derivedFrom":subQ0})])]})]})})]});}
            var Q11;
            {var subQ0=sQuery(id+"F7.wireOp",EDGE,"E39");var subQ1=sQuery(id+"F7.wireOp",EDGE,"E45.1.1");Q11=makeQuery(id+"F10.opFillet","BLEND_EDGE",EDGE,{"blendedFrom":[makeQuery(id+"F8.boolean.opBoolean","INTERSECT",EDGE,{"derivedFrom":[makeQuery(id+"F1.opRevolve","SWEPT_FACE",FACE,{"disambiguationData":[OSD([sQuery(id+"F0.wireOp",EDGE,"E35")])]}),makeQuery(id+"F8.opExtrude","SWEPT_FACE",FACE,{"disambiguationData":[OSD([subQ1])]})]}),makeQuery(id+"F9.opFillet","SPLIT",FACE,{"disambiguationData":[OD(2.0)],"derivedFrom":makeQuery(id+"F8.boolean.opBoolean","MERGE",FACE,{"derivedFrom":[makeQuery(id+"F1.opRevolve","SWEPT_FACE",FACE,{"disambiguationData":[OSD([sQuery(id+"F0.wireOp",EDGE,"E36")])]}),makeQuery(id+"F8.opExtrude","SWEPT_FACE",FACE,{"disambiguationData":[OSD([subQ0]),TDD([makeQuery(id+"F7.imprint","IMPRINT",EDGE,{"disambiguationData":[TD([[makeQuery(id+"F7.imprint","INTERSECT",VERTEX,{"derivedFrom":[subQ0,sQuery(id+"F7.wireOp",EDGE,"E45.3.1")]}),-1.0]])],"derivedFrom":subQ0})])]}),makeQuery(id+"F8.opExtrude","SWEPT_FACE",FACE,{"disambiguationData":[OSD([subQ0]),TDD([makeQuery(id+"F7.imprint","IMPRINT",EDGE,{"disambiguationData":[TD([[makeQuery(id+"F7.imprint","INTERSECT",VERTEX,{"derivedFrom":[subQ0,sQuery(id+"F7.wireOp",EDGE,"E45.4.1")]}),-1.0]])],"derivedFrom":subQ0})])]}),makeQuery(id+"F8.opExtrude","SWEPT_FACE",FACE,{"disambiguationData":[OSD([subQ0]),TDD([makeQuery(id+"F7.imprint","IMPRINT",EDGE,{"disambiguationData":[TD([[makeQuery(id+"F7.imprint","INTERSECT",VERTEX,{"derivedFrom":[subQ0,sQuery(id+"F7.wireOp",EDGE,"E43")]}),1.0]])],"derivedFrom":subQ0})])]}),makeQuery(id+"F8.opExtrude","SWEPT_FACE",FACE,{"disambiguationData":[OSD([subQ0]),TDD([makeQuery(id+"F7.imprint","IMPRINT",EDGE,{"disambiguationData":[TD([[makeQuery(id+"F7.imprint","INTERSECT",VERTEX,{"derivedFrom":[subQ0,sQuery(id+"F7.wireOp",EDGE,"E44")]}),-1.0]])],"derivedFrom":subQ0})])]}),makeQuery(id+"F8.opExtrude","SWEPT_FACE",FACE,{"disambiguationData":[OSD([subQ0]),TDD([makeQuery(id+"F7.imprint","IMPRINT",EDGE,{"disambiguationData":[TD([[makeQuery(id+"F7.imprint","INTERSECT",VERTEX,{"derivedFrom":[subQ0,subQ1]}),-1.0]])],"derivedFrom":subQ0})])]}),makeQuery(id+"F8.opExtrude","SWEPT_FACE",FACE,{"disambiguationData":[OSD([subQ0]),TDD([makeQuery(id+"F7.imprint","IMPRINT",EDGE,{"disambiguationData":[TD([[makeQuery(id+"F7.imprint","INTERSECT",VERTEX,{"derivedFrom":[subQ0,sQuery(id+"F7.wireOp",EDGE,"E45.2.1")]}),-1.0]])],"derivedFrom":subQ0})])]})]})})],"blendedInto":[makeQuery(id+"F9.opFillet","SPLIT",FACE,{"disambiguationData":[OD(2.0)],"derivedFrom":makeQuery(id+"F8.boolean.opBoolean","MERGE",FACE,{"derivedFrom":[makeQuery(id+"F1.opRevolve","SWEPT_FACE",FACE,{"disambiguationData":[OSD([sQuery(id+"F0.wireOp",EDGE,"E36")])]}),makeQuery(id+"F8.opExtrude","SWEPT_FACE",FACE,{"disambiguationData":[OSD([subQ0]),TDD([makeQuery(id+"F7.imprint","IMPRINT",EDGE,{"disambiguationData":[TD([[makeQuery(id+"F7.imprint","INTERSECT",VERTEX,{"derivedFrom":[subQ0,sQuery(id+"F7.wireOp",EDGE,"E45.3.1")]}),-1.0]])],"derivedFrom":subQ0})])]}),makeQuery(id+"F8.opExtrude","SWEPT_FACE",FACE,{"disambiguationData":[OSD([subQ0]),TDD([makeQuery(id+"F7.imprint","IMPRINT",EDGE,{"disambiguationData":[TD([[makeQuery(id+"F7.imprint","INTERSECT",VERTEX,{"derivedFrom":[subQ0,sQuery(id+"F7.wireOp",EDGE,"E45.4.1")]}),-1.0]])],"derivedFrom":subQ0})])]}),makeQuery(id+"F8.opExtrude","SWEPT_FACE",FACE,{"disambiguationData":[OSD([subQ0]),TDD([makeQuery(id+"F7.imprint","IMPRINT",EDGE,{"disambiguationData":[TD([[makeQuery(id+"F7.imprint","INTERSECT",VERTEX,{"derivedFrom":[subQ0,sQuery(id+"F7.wireOp",EDGE,"E43")]}),1.0]])],"derivedFrom":subQ0})])]}),makeQuery(id+"F8.opExtrude","SWEPT_FACE",FACE,{"disambiguationData":[OSD([subQ0]),TDD([makeQuery(id+"F7.imprint","IMPRINT",EDGE,{"disambiguationData":[TD([[makeQuery(id+"F7.imprint","INTERSECT",VERTEX,{"derivedFrom":[subQ0,sQuery(id+"F7.wireOp",EDGE,"E44")]}),-1.0]])],"derivedFrom":subQ0})])]}),makeQuery(id+"F8.opExtrude","SWEPT_FACE",FACE,{"disambiguationData":[OSD([subQ0]),TDD([makeQuery(id+"F7.imprint","IMPRINT",EDGE,{"disambiguationData":[TD([[makeQuery(id+"F7.imprint","INTERSECT",VERTEX,{"derivedFrom":[subQ0,subQ1]}),-1.0]])],"derivedFrom":subQ0})])]}),makeQuery(id+"F8.opExtrude","SWEPT_FACE",FACE,{"disambiguationData":[OSD([subQ0]),TDD([makeQuery(id+"F7.imprint","IMPRINT",EDGE,{"disambiguationData":[TD([[makeQuery(id+"F7.imprint","INTERSECT",VERTEX,{"derivedFrom":[subQ0,sQuery(id+"F7.wireOp",EDGE,"E45.2.1")]}),-1.0]])],"derivedFrom":subQ0})])]})]})})]});}
            fillet(context, id + "F11", {"entities" : qUnion([Q0, Q1, Q2, Q3, Q4, Q5, Q6, Q7, Q8, Q9, Q10, Q11]), "radius" : 1 * mm, "tangentPropagation" : true, "allowEdgeOverflow" : false});
        }
    });
